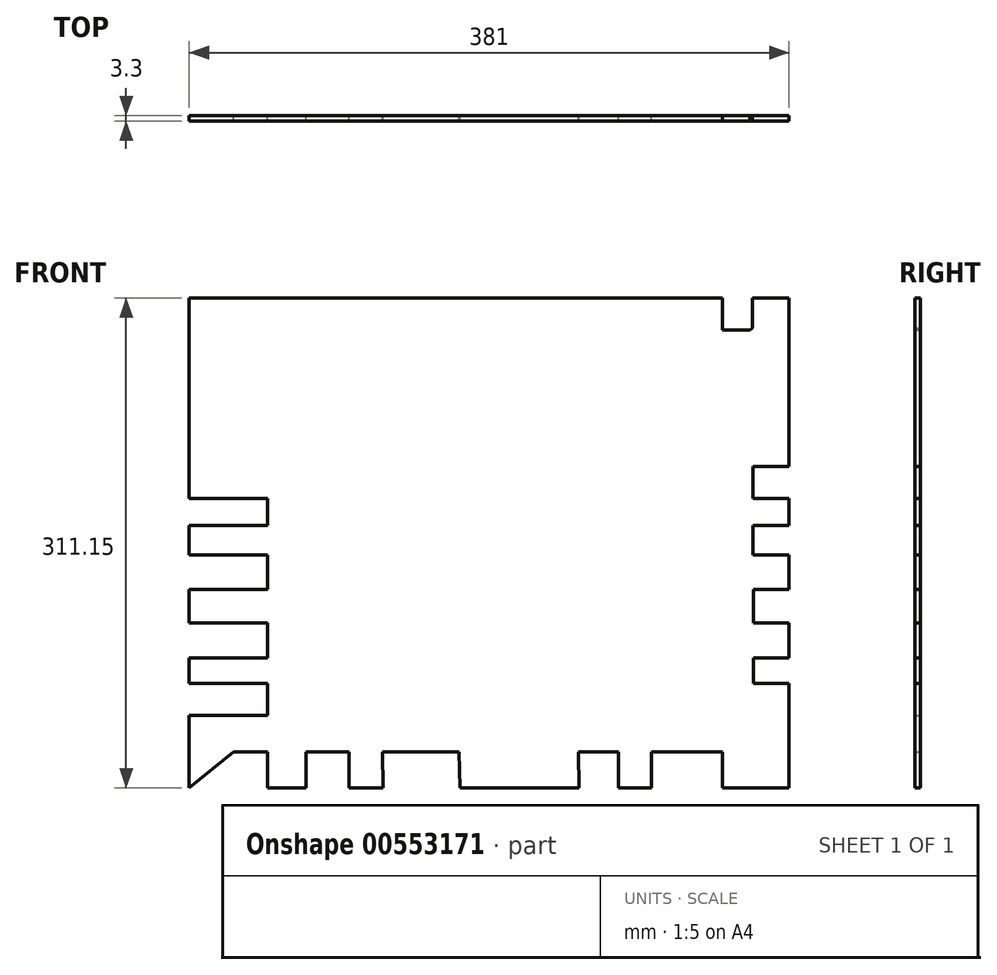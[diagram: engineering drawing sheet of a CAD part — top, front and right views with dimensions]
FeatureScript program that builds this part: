
annotation { "Feature Type Name" : "Feature", "Feature Type Description" : "" }
export const myFeature = defineFeature(function(context is Context, id is Id, definition is map)
    precondition{}
    {
        {
            var Q0;
            Q0=qCreatedBy(makeId("Front.planeOp"),FACE);
            var sketch = newSketch(context, id + "F0", { "sketchPlane" : qUnion([Q0])});
            skLineSegment(sketch, "E0.bottom", {"start": v(190.5, 155.58) * mm, "end": v(-190.5, 155.58) * mm});
            skLineSegment(sketch, "E0.top", {"start": v(190.5, -155.58) * mm, "end": v(-190.5, -155.58) * mm});
            skLineSegment(sketch, "E0.left", {"start": v(190.5, 155.58) * mm, "end": v(190.5, -155.58) * mm});
            skLineSegment(sketch, "E0.right", {"start": v(-190.5, 155.58) * mm, "end": v(-190.5, -155.58) * mm});
            skPoint(sketch, "E0.middle", {"position": v(0, 0) * mm});
            skLineSegment(sketch, "E1", {"start": v(-190.5, 155.58) * mm, "end": v(190.5, -155.57) * mm});
            skLineSegment(sketch, "E2", {"start": v(-190.5, -155.58) * mm, "end": v(190.5, 155.58) * mm});
            skLineSegment(sketch, "E3", {"start": v(-190.5, 135.33) * mm, "end": v(190.5, 135.33) * mm});
            skLineSegment(sketch, "E4", {"start": v(-190.5, 112.36) * mm, "end": v(190.5, 112.36) * mm});
            skLineSegment(sketch, "E5", {"start": v(-190.5, 91.1) * mm, "end": v(190.5, 91.1) * mm});
            skLineSegment(sketch, "E6", {"start": v(-190.5, 70.67) * mm, "end": v(190.5, 70.67) * mm});
            skLineSegment(sketch, "E7", {"start": v(-190.5, 48.55) * mm, "end": v(190.5, 48.55) * mm});
            skLineSegment(sketch, "E8", {"start": v(190.5, 48.55) * mm, "end": v(190.5, 28.13) * mm});
            skLineSegment(sketch, "E9", {"start": v(190.5, 28.13) * mm, "end": v(-190.5, 28.13) * mm});
            skLineSegment(sketch, "E10", {"start": v(-190.5, 28.13) * mm, "end": v(-190.5, 11.12) * mm});
            skLineSegment(sketch, "E11", {"start": v(-190.5, 11.12) * mm, "end": v(190.5, 11.12) * mm});
            skLineSegment(sketch, "E12", {"start": v(190.5, 11.12) * mm, "end": v(190.5, -7.6) * mm});
            skLineSegment(sketch, "E13", {"start": v(190.5, -7.6) * mm, "end": v(-190.5, -7.6) * mm});
            skLineSegment(sketch, "E14", {"start": v(-190.5, -7.6) * mm, "end": v(-190.5, -29.72) * mm});
            skLineSegment(sketch, "E15", {"start": v(-190.5, -29.72) * mm, "end": v(190.5, -29.72) * mm});
            skLineSegment(sketch, "E16", {"start": v(190.5, -29.72) * mm, "end": v(190.5, -50.99) * mm});
            skLineSegment(sketch, "E17", {"start": v(190.5, -50.99) * mm, "end": v(-190.5, -50.99) * mm});
            skLineSegment(sketch, "E18", {"start": v(-190.5, -50.99) * mm, "end": v(-190.5, -73.1) * mm});
            skLineSegment(sketch, "E19", {"start": v(-190.5, -73.1) * mm, "end": v(190.5, -73.1) * mm});
            skLineSegment(sketch, "E20", {"start": v(190.5, -73.1) * mm, "end": v(190.5, -89.27) * mm});
            skLineSegment(sketch, "E21", {"start": v(190.5, -89.27) * mm, "end": v(-190.5, -89.27) * mm});
            skLineSegment(sketch, "E22", {"start": v(-190.5, -89.27) * mm, "end": v(-190.5, -109.69) * mm});
            skLineSegment(sketch, "E23", {"start": v(-190.5, -109.69) * mm, "end": v(190.5, -109.69) * mm});
            skLineSegment(sketch, "E24", {"start": v(-190.5, -132.66) * mm, "end": v(190.5, -132.66) * mm});
            skLineSegment(sketch, "E25", {"start": v(96.32, 155.58) * mm, "end": v(50.38, 155.58) * mm});
            skLineSegment(sketch, "E26", {"start": v(9.5, 155.58) * mm, "end": v(-36.4, 155.58) * mm});
            skLineSegment(sketch, "E27", {"start": v(-81.1, 155.58) * mm, "end": v(-116.39, 155.58) * mm});
            skLineSegment(sketch, "E28", {"start": v(148.22, -155.58) * mm, "end": v(103.13, -155.58) * mm});
            skLineSegment(sketch, "E29", {"start": v(57.18, -155.58) * mm, "end": v(7.83, -155.58) * mm});
            skLineSegment(sketch, "E30", {"start": v(-35.56, -155.58) * mm, "end": v(-81.1, -155.58) * mm});
            skLineSegment(sketch, "E31", {"start": v(168.09, -155.58) * mm, "end": v(141.17, -155.58) * mm});
            skLineSegment(sketch, "E32", {"start": v(148.22, 155.58) * mm, "end": v(125.53, 155.58) * mm});
            skLineSegment(sketch, "E33", {"start": v(125.53, -155.58) * mm, "end": v(103.13, -155.58) * mm});
            skLineSegment(sketch, "E34", {"start": v(103.13, 155.58) * mm, "end": v(82.1, 155.58) * mm});
            skLineSegment(sketch, "E35", {"start": v(82.1, -155.58) * mm, "end": v(63.87, -155.58) * mm});
            skLineSegment(sketch, "E36", {"start": v(159.4, 155.58) * mm, "end": v(136.88, 155.58) * mm});
            skLineSegment(sketch, "E37", {"start": v(136.88, 155.58) * mm, "end": v(111.64, 155.58) * mm});
            skLineSegment(sketch, "E38", {"start": v(111.64, 155.58) * mm, "end": v(82.1, 155.58) * mm});
            skLineSegment(sketch, "E39", {"start": v(65.6, 155.58) * mm, "end": v(37.82, 155.58) * mm});
            skLineSegment(sketch, "E40", {"start": v(37.82, 155.58) * mm, "end": v(9.5, 155.58) * mm});
            skLineSegment(sketch, "E41", {"start": v(-13.45, 155.58) * mm, "end": v(-36.4, 155.58) * mm});
            skLineSegment(sketch, "E42", {"start": v(-63.8, 155.58) * mm, "end": v(-98.74, 155.58) * mm});
            skLineSegment(sketch, "E43", {"start": v(-98.74, 155.58) * mm, "end": v(-128.06, 155.58) * mm});
            skLineSegment(sketch, "E44", {"start": v(-128.06, 155.58) * mm, "end": v(-153.25, 155.58) * mm});
            skLineSegment(sketch, "E45", {"start": v(-153.25, 155.58) * mm, "end": v(-169.75, 155.58) * mm});
            skLineSegment(sketch, "E46", {"start": v(-169.75, 155.58) * mm, "end": v(159.4, 155.58) * mm});
            skLineSegment(sketch, "E47", {"start": v(167.22, 155.58) * mm, "end": v(168.09, -155.58) * mm});
            skLineSegment(sketch, "E48", {"start": v(148.22, 155.58) * mm, "end": v(148.22, -155.58) * mm});
            skLineSegment(sketch, "E49", {"start": v(125.53, 155.58) * mm, "end": v(125.53, -155.58) * mm});
            skLineSegment(sketch, "E50", {"start": v(103.13, 155.58) * mm, "end": v(103.13, -155.58) * mm});
            skLineSegment(sketch, "E51", {"start": v(82.1, 155.58) * mm, "end": v(82.1, -155.58) * mm});
            skLineSegment(sketch, "E52", {"start": v(50.38, 155.58) * mm, "end": v(57.18, -155.57) * mm});
            skLineSegment(sketch, "E53", {"start": v(23.66, 155.58) * mm, "end": v(32.5, -155.58) * mm});
            skLineSegment(sketch, "E54", {"start": v(0, 155.58) * mm, "end": v(7.83, -155.58) * mm});
            skLineSegment(sketch, "E55", {"start": v(-24.93, 155.58) * mm, "end": v(-18.64, -155.58) * mm});
            skLineSegment(sketch, "E56", {"start": v(-44.7, -155.58) * mm, "end": v(-67.27, -155.58) * mm});
            skLineSegment(sketch, "E57", {"start": v(-88.98, -155.58) * mm, "end": v(-108.96, -155.58) * mm});
            skLineSegment(sketch, "E58", {"start": v(-108.96, 155.58) * mm, "end": v(-128.06, 155.58) * mm});
            skLineSegment(sketch, "E59", {"start": v(-153.25, -155.58) * mm, "end": v(-174.1, -155.58) * mm});
            skLineSegment(sketch, "E60", {"start": v(-50.77, 155.58) * mm, "end": v(-44.7, -155.58) * mm});
            skLineSegment(sketch, "E61", {"start": v(-72.48, 155.58) * mm, "end": v(-67.27, -155.58) * mm});
            skLineSegment(sketch, "E62", {"start": v(-89.85, 155.58) * mm, "end": v(-88.98, -155.58) * mm});
            skLineSegment(sketch, "E63", {"start": v(-116.39, 155.58) * mm, "end": v(-116.39, -155.58) * mm});
            skLineSegment(sketch, "E64", {"start": v(-140.66, 155.58) * mm, "end": v(-140.66, -155.58) * mm});
            skSolve(sketch);
        }
        {
            var Q0;
            {var subQ0=sQuery(id+"F0.wireOp",EDGE,"E60");var subQ1=sQuery(id+"F0.wireOp",EDGE,"E13");var subQ2=makeQuery(id+"F0.imprint","INTERSECT",VERTEX,{"derivedFrom":[subQ1,subQ0]});Q0=makeQuery(id+"F0.imprint","IMPRINT",FACE,{"disambiguationData":[TD([[makeQuery(id+"F0.imprint","IMPRINT",EDGE,{"disambiguationData":[TD([[subQ2,-1.0]])],"derivedFrom":subQ1}),1.0]])]});}
            var Q1;
            {var subQ0=sQuery(id+"F0.wireOp",EDGE,"E4");var subQ1=sQuery(id+"F0.wireOp",EDGE,"E0.left");var subQ2=makeQuery(id+"F0.imprint","INTERSECT",VERTEX,{"derivedFrom":[subQ1,subQ0]});Q1=makeQuery(id+"F0.imprint","IMPRINT",FACE,{"disambiguationData":[TD([[makeQuery(id+"F0.imprint","IMPRINT",EDGE,{"disambiguationData":[TD([[subQ2,-1.0]])],"derivedFrom":subQ1}),-1.0]])]});}
            var Q2;
            {var subQ0=sQuery(id+"F0.wireOp",EDGE,"E54");var subQ1=sQuery(id+"F0.wireOp",EDGE,"E23");var subQ2=makeQuery(id+"F0.imprint","INTERSECT",VERTEX,{"derivedFrom":[subQ1,subQ0]});Q2=makeQuery(id+"F0.imprint","IMPRINT",FACE,{"disambiguationData":[TD([[makeQuery(id+"F0.imprint","IMPRINT",EDGE,{"disambiguationData":[TD([[subQ2,-1.0]])],"derivedFrom":subQ1}),-1.0]])]});}
            var Q3;
            {var subQ0=sQuery(id+"F0.wireOp",EDGE,"E52");var subQ1=sQuery(id+"F0.wireOp",EDGE,"E19");var subQ2=makeQuery(id+"F0.imprint","INTERSECT",VERTEX,{"derivedFrom":[subQ1,subQ0]});Q3=makeQuery(id+"F0.imprint","IMPRINT",FACE,{"disambiguationData":[TD([[makeQuery(id+"F0.imprint","IMPRINT",EDGE,{"disambiguationData":[TD([[subQ2,-1.0]])],"derivedFrom":subQ1}),-1.0]])]});}
            var Q4;
            {var subQ0=sQuery(id+"F0.wireOp",EDGE,"E60");var subQ1=sQuery(id+"F0.wireOp",EDGE,"E6");var subQ2=makeQuery(id+"F0.imprint","INTERSECT",VERTEX,{"derivedFrom":[subQ1,subQ0]});Q4=makeQuery(id+"F0.imprint","IMPRINT",FACE,{"disambiguationData":[TD([[makeQuery(id+"F0.imprint","IMPRINT",EDGE,{"disambiguationData":[TD([[subQ2,-1.0]])],"derivedFrom":subQ1}),-1.0]])]});}
            var Q5;
            {var subQ0=sQuery(id+"F0.wireOp",EDGE,"E48");var subQ1=sQuery(id+"F0.wireOp",EDGE,"E17");var subQ2=makeQuery(id+"F0.imprint","INTERSECT",VERTEX,{"derivedFrom":[subQ1,subQ0]});Q5=makeQuery(id+"F0.imprint","IMPRINT",FACE,{"disambiguationData":[TD([[makeQuery(id+"F0.imprint","IMPRINT",EDGE,{"disambiguationData":[TD([[subQ2,-1.0]])],"derivedFrom":subQ1}),1.0]])]});}
            var Q6;
            {var subQ0=sQuery(id+"F0.wireOp",EDGE,"E53");var subQ1=sQuery(id+"F0.wireOp",EDGE,"E4");var subQ2=makeQuery(id+"F0.imprint","INTERSECT",VERTEX,{"derivedFrom":[subQ1,subQ0]});Q6=makeQuery(id+"F0.imprint","IMPRINT",FACE,{"disambiguationData":[TD([[makeQuery(id+"F0.imprint","IMPRINT",EDGE,{"disambiguationData":[TD([[subQ2,-1.0]])],"derivedFrom":subQ1}),-1.0]])]});}
            var Q7;
            {var subQ0=sQuery(id+"F0.wireOp",EDGE,"E6");var subQ1=sQuery(id+"F0.wireOp",EDGE,"E2");var subQ2=makeQuery(id+"F0.imprint","INTERSECT",VERTEX,{"derivedFrom":[subQ1,subQ0]});Q7=makeQuery(id+"F0.imprint","IMPRINT",FACE,{"disambiguationData":[TD([[makeQuery(id+"F0.imprint","IMPRINT",EDGE,{"disambiguationData":[TD([[subQ2,-1.0]])],"derivedFrom":subQ1}),-1.0]])]});}
            var Q8;
            {var subQ0=sQuery(id+"F0.wireOp",EDGE,"E53");var subQ1=sQuery(id+"F0.wireOp",EDGE,"E11");var subQ2=makeQuery(id+"F0.imprint","INTERSECT",VERTEX,{"derivedFrom":[subQ1,subQ0]});Q8=makeQuery(id+"F0.imprint","IMPRINT",FACE,{"disambiguationData":[TD([[makeQuery(id+"F0.imprint","IMPRINT",EDGE,{"disambiguationData":[TD([[subQ2,-1.0]])],"derivedFrom":subQ1}),-1.0]])]});}
            var Q9;
            {var subQ0=sQuery(id+"F0.wireOp",EDGE,"E54");var subQ1=sQuery(id+"F0.wireOp",EDGE,"E19");var subQ2=makeQuery(id+"F0.imprint","INTERSECT",VERTEX,{"derivedFrom":[subQ1,subQ0]});Q9=makeQuery(id+"F0.imprint","IMPRINT",FACE,{"disambiguationData":[TD([[makeQuery(id+"F0.imprint","IMPRINT",EDGE,{"disambiguationData":[TD([[subQ2,-1.0]])],"derivedFrom":subQ1}),-1.0]])]});}
            var Q10;
            {var subQ0=sQuery(id+"F0.wireOp",EDGE,"E15");var subQ1=sQuery(id+"F0.wireOp",EDGE,"E2");var subQ2=makeQuery(id+"F0.imprint","INTERSECT",VERTEX,{"derivedFrom":[subQ1,subQ0]});Q10=makeQuery(id+"F0.imprint","IMPRINT",FACE,{"disambiguationData":[TD([[makeQuery(id+"F0.imprint","IMPRINT",EDGE,{"disambiguationData":[TD([[subQ2,-1.0]])],"derivedFrom":subQ1}),-1.0]])]});}
            var Q11;
            {var subQ0=sQuery(id+"F0.wireOp",EDGE,"E52");var subQ1=sQuery(id+"F0.wireOp",EDGE,"E3");var subQ2=makeQuery(id+"F0.imprint","INTERSECT",VERTEX,{"derivedFrom":[subQ1,subQ0]});Q11=makeQuery(id+"F0.imprint","IMPRINT",FACE,{"disambiguationData":[TD([[makeQuery(id+"F0.imprint","IMPRINT",EDGE,{"disambiguationData":[TD([[subQ2,-1.0]])],"derivedFrom":subQ1}),1.0]])]});}
            var Q12;
            {var subQ0=sQuery(id+"F0.wireOp",EDGE,"E53");var subQ1=sQuery(id+"F0.wireOp",EDGE,"E19");var subQ2=makeQuery(id+"F0.imprint","INTERSECT",VERTEX,{"derivedFrom":[subQ1,subQ0]});Q12=makeQuery(id+"F0.imprint","IMPRINT",FACE,{"disambiguationData":[TD([[makeQuery(id+"F0.imprint","IMPRINT",EDGE,{"disambiguationData":[TD([[subQ2,-1.0]])],"derivedFrom":subQ1}),-1.0]])]});}
            var Q13;
            {var subQ0=sQuery(id+"F0.wireOp",EDGE,"E5");var subQ1=sQuery(id+"F0.wireOp",EDGE,"E1");var subQ2=makeQuery(id+"F0.imprint","INTERSECT",VERTEX,{"derivedFrom":[subQ1,subQ0]});Q13=makeQuery(id+"F0.imprint","IMPRINT",FACE,{"disambiguationData":[TD([[makeQuery(id+"F0.imprint","IMPRINT",EDGE,{"disambiguationData":[TD([[subQ2,-1.0]])],"derivedFrom":subQ1}),1.0]])]});}
            var Q14;
            {var subQ0=sQuery(id+"F0.wireOp",EDGE,"E47");var subQ1=sQuery(id+"F0.wireOp",EDGE,"E21");var subQ2=makeQuery(id+"F0.imprint","INTERSECT",VERTEX,{"derivedFrom":[subQ1,subQ0]});Q14=makeQuery(id+"F0.imprint","IMPRINT",FACE,{"disambiguationData":[TD([[makeQuery(id+"F0.imprint","IMPRINT",EDGE,{"disambiguationData":[TD([[subQ2,-1.0]])],"derivedFrom":subQ1}),1.0]])]});}
            var Q15;
            {var subQ0=sQuery(id+"F0.wireOp",EDGE,"E50");var subQ1=sQuery(id+"F0.wireOp",EDGE,"E7");var subQ2=makeQuery(id+"F0.imprint","INTERSECT",VERTEX,{"derivedFrom":[subQ1,subQ0]});Q15=makeQuery(id+"F0.imprint","IMPRINT",FACE,{"disambiguationData":[TD([[makeQuery(id+"F0.imprint","IMPRINT",EDGE,{"disambiguationData":[TD([[subQ2,-1.0]])],"derivedFrom":subQ1}),-1.0]])]});}
            var Q16;
            {var subQ1=sQuery(id+"F0.wireOp",EDGE,"E2");var subQ7=sQuery(id+"F0.wireOp",EDGE,"E6");var subQ8=makeQuery(id+"F0.imprint","INTERSECT",VERTEX,{"derivedFrom":[subQ1,subQ7]});Q16=makeQuery(id+"F0.imprint","IMPRINT",FACE,{"disambiguationData":[TD([[makeQuery(id+"F0.imprint","IMPRINT",EDGE,{"disambiguationData":[TD([[subQ8,-1.0]])],"derivedFrom":subQ1}),1.0]])]});}
            var Q17;
            {var subQ5=sQuery(id+"F0.wireOp",EDGE,"E46");var subQ6=sQuery(id+"F0.wireOp",EDGE,"E0.bottom");var subQ7=makeQuery(id+"F0.imprint","INTERSECT",VERTEX,{"disambiguationData":[OD(1.0)],"derivedFrom":[subQ6,subQ5]});Q17=makeQuery(id+"F0.imprint","IMPRINT",FACE,{"disambiguationData":[TD([[makeQuery(id+"F0.imprint","IMPRINT",EDGE,{"disambiguationData":[TD([[subQ7,1.0]])],"derivedFrom":subQ6}),1.0]])]});}
            var Q18;
            {var subQ0=sQuery(id+"F0.wireOp",EDGE,"E11");var subQ5=sQuery(id+"F0.wireOp",EDGE,"E64");var subQ6=makeQuery(id+"F0.imprint","INTERSECT",VERTEX,{"derivedFrom":[subQ0,subQ5]});Q18=makeQuery(id+"F0.imprint","IMPRINT",FACE,{"disambiguationData":[TD([[makeQuery(id+"F0.imprint","IMPRINT",EDGE,{"disambiguationData":[TD([[subQ6,-1.0]])],"derivedFrom":subQ5}),-1.0]])]});}
            var Q19;
            {var subQ0=sQuery(id+"F0.wireOp",EDGE,"E51");var subQ1=sQuery(id+"F0.wireOp",EDGE,"E3");var subQ2=makeQuery(id+"F0.imprint","INTERSECT",VERTEX,{"derivedFrom":[subQ1,subQ0]});Q19=makeQuery(id+"F0.imprint","IMPRINT",FACE,{"disambiguationData":[TD([[makeQuery(id+"F0.imprint","IMPRINT",EDGE,{"disambiguationData":[TD([[subQ2,-1.0]])],"derivedFrom":subQ1}),1.0]])]});}
            var Q20;
            {var subQ5=sQuery(id+"F0.wireOp",EDGE,"E1");var subQ7=sQuery(id+"F0.wireOp",EDGE,"E63");var subQ9=makeQuery(id+"F0.imprint","INTERSECT",VERTEX,{"derivedFrom":[subQ5,subQ7]});Q20=makeQuery(id+"F0.imprint","IMPRINT",FACE,{"disambiguationData":[TD([[makeQuery(id+"F0.imprint","IMPRINT",EDGE,{"disambiguationData":[TD([[subQ9,-1.0]])],"derivedFrom":subQ5}),1.0]])]});}
            var Q21;
            {var subQ0=sQuery(id+"F0.wireOp",EDGE,"E48");var subQ1=sQuery(id+"F0.wireOp",EDGE,"E7");var subQ2=makeQuery(id+"F0.imprint","INTERSECT",VERTEX,{"derivedFrom":[subQ1,subQ0]});Q21=makeQuery(id+"F0.imprint","IMPRINT",FACE,{"disambiguationData":[TD([[makeQuery(id+"F0.imprint","IMPRINT",EDGE,{"disambiguationData":[TD([[subQ2,-1.0]])],"derivedFrom":subQ1}),-1.0]])]});}
            var Q22;
            {var subQ0=sQuery(id+"F0.wireOp",EDGE,"E12");Q22=makeQuery(id+"F0.imprint","IMPRINT",FACE,{"disambiguationData":[TD([[makeQuery(id+"F0.imprint","IMPRINT",EDGE,{"derivedFrom":subQ0}),-1.0]])]});}
            var Q23;
            {var subQ0=sQuery(id+"F0.wireOp",EDGE,"E24");var subQ3=sQuery(id+"F0.wireOp",EDGE,"E2");var subQ4=makeQuery(id+"F0.imprint","INTERSECT",VERTEX,{"derivedFrom":[subQ3,subQ0]});Q23=makeQuery(id+"F0.imprint","IMPRINT",FACE,{"disambiguationData":[TD([[makeQuery(id+"F0.imprint","IMPRINT",EDGE,{"disambiguationData":[TD([[subQ4,-1.0]])],"derivedFrom":subQ3}),1.0]])]});}
            var Q24;
            {var subQ0=sQuery(id+"F0.wireOp",EDGE,"E52");var subQ1=sQuery(id+"F0.wireOp",EDGE,"E11");var subQ2=makeQuery(id+"F0.imprint","INTERSECT",VERTEX,{"derivedFrom":[subQ1,subQ0]});Q24=makeQuery(id+"F0.imprint","IMPRINT",FACE,{"disambiguationData":[TD([[makeQuery(id+"F0.imprint","IMPRINT",EDGE,{"disambiguationData":[TD([[subQ2,-1.0]])],"derivedFrom":subQ1}),-1.0]])]});}
            var Q25;
            {var subQ3=sQuery(id+"F0.wireOp",EDGE,"E24");var subQ7=sQuery(id+"F0.wireOp",EDGE,"E62");var subQ8=makeQuery(id+"F0.imprint","INTERSECT",VERTEX,{"derivedFrom":[subQ3,subQ7]});Q25=makeQuery(id+"F0.imprint","IMPRINT",FACE,{"disambiguationData":[TD([[makeQuery(id+"F0.imprint","IMPRINT",EDGE,{"disambiguationData":[TD([[subQ8,-1.0]])],"derivedFrom":subQ3}),-1.0]])]});}
            var Q26;
            {var subQ1=sQuery(id+"F0.wireOp",EDGE,"E1");var subQ7=sQuery(id+"F0.wireOp",EDGE,"E19");var subQ8=makeQuery(id+"F0.imprint","INTERSECT",VERTEX,{"derivedFrom":[subQ1,subQ7]});Q26=makeQuery(id+"F0.imprint","IMPRINT",FACE,{"disambiguationData":[TD([[makeQuery(id+"F0.imprint","IMPRINT",EDGE,{"disambiguationData":[TD([[subQ8,-1.0]])],"derivedFrom":subQ1}),-1.0]])]});}
            var Q27;
            {var subQ0=sQuery(id+"F0.wireOp",EDGE,"E61");var subQ1=sQuery(id+"F0.wireOp",EDGE,"E21");var subQ2=makeQuery(id+"F0.imprint","INTERSECT",VERTEX,{"derivedFrom":[subQ1,subQ0]});Q27=makeQuery(id+"F0.imprint","IMPRINT",FACE,{"disambiguationData":[TD([[makeQuery(id+"F0.imprint","IMPRINT",EDGE,{"disambiguationData":[TD([[subQ2,-1.0]])],"derivedFrom":subQ1}),1.0]])]});}
            var Q28;
            {var subQ0=sQuery(id+"F0.wireOp",EDGE,"E24");var subQ1=sQuery(id+"F0.wireOp",EDGE,"E2");var subQ2=makeQuery(id+"F0.imprint","INTERSECT",VERTEX,{"derivedFrom":[subQ1,subQ0]});Q28=makeQuery(id+"F0.imprint","IMPRINT",FACE,{"disambiguationData":[TD([[makeQuery(id+"F0.imprint","IMPRINT",EDGE,{"disambiguationData":[TD([[subQ2,-1.0]])],"derivedFrom":subQ1}),-1.0]])]});}
            var Q29;
            {var subQ0=sQuery(id+"F0.wireOp",EDGE,"E23");var subQ1=sQuery(id+"F0.wireOp",EDGE,"E0.left");var subQ2=makeQuery(id+"F0.imprint","INTERSECT",VERTEX,{"derivedFrom":[subQ1,subQ0]});Q29=makeQuery(id+"F0.imprint","IMPRINT",FACE,{"disambiguationData":[TD([[makeQuery(id+"F0.imprint","IMPRINT",EDGE,{"disambiguationData":[TD([[subQ2,-1.0]])],"derivedFrom":subQ1}),-1.0]])]});}
            var Q30;
            {var subQ0=sQuery(id+"F0.wireOp",EDGE,"E60");var subQ1=sQuery(id+"F0.wireOp",EDGE,"E5");var subQ2=makeQuery(id+"F0.imprint","INTERSECT",VERTEX,{"derivedFrom":[subQ1,subQ0]});Q30=makeQuery(id+"F0.imprint","IMPRINT",FACE,{"disambiguationData":[TD([[makeQuery(id+"F0.imprint","IMPRINT",EDGE,{"disambiguationData":[TD([[subQ2,-1.0]])],"derivedFrom":subQ1}),-1.0]])]});}
            var Q31;
            {var subQ0=sQuery(id+"F0.wireOp",EDGE,"E62");var subQ1=sQuery(id+"F0.wireOp",EDGE,"E3");var subQ2=makeQuery(id+"F0.imprint","INTERSECT",VERTEX,{"derivedFrom":[subQ1,subQ0]});Q31=makeQuery(id+"F0.imprint","IMPRINT",FACE,{"disambiguationData":[TD([[makeQuery(id+"F0.imprint","IMPRINT",EDGE,{"disambiguationData":[TD([[subQ2,-1.0]])],"derivedFrom":subQ1}),1.0]])]});}
            var Q32;
            {var subQ0=sQuery(id+"F0.wireOp",EDGE,"E4");var subQ1=sQuery(id+"F0.wireOp",EDGE,"E1");var subQ2=makeQuery(id+"F0.imprint","INTERSECT",VERTEX,{"derivedFrom":[subQ1,subQ0]});Q32=makeQuery(id+"F0.imprint","IMPRINT",FACE,{"disambiguationData":[TD([[makeQuery(id+"F0.imprint","IMPRINT",EDGE,{"disambiguationData":[TD([[subQ2,-1.0]])],"derivedFrom":subQ1}),1.0]])]});}
            var Q33;
            {var subQ0=sQuery(id+"F0.wireOp",EDGE,"E53");var subQ1=sQuery(id+"F0.wireOp",EDGE,"E23");var subQ2=makeQuery(id+"F0.imprint","INTERSECT",VERTEX,{"derivedFrom":[subQ1,subQ0]});Q33=makeQuery(id+"F0.imprint","IMPRINT",FACE,{"disambiguationData":[TD([[makeQuery(id+"F0.imprint","IMPRINT",EDGE,{"disambiguationData":[TD([[subQ2,-1.0]])],"derivedFrom":subQ1}),-1.0]])]});}
            var Q34;
            {var subQ0=sQuery(id+"F0.wireOp",EDGE,"E50");var subQ1=sQuery(id+"F0.wireOp",EDGE,"E21");var subQ2=makeQuery(id+"F0.imprint","INTERSECT",VERTEX,{"derivedFrom":[subQ1,subQ0]});Q34=makeQuery(id+"F0.imprint","IMPRINT",FACE,{"disambiguationData":[TD([[makeQuery(id+"F0.imprint","IMPRINT",EDGE,{"disambiguationData":[TD([[subQ2,-1.0]])],"derivedFrom":subQ1}),1.0]])]});}
            var Q35;
            {var subQ0=sQuery(id+"F0.wireOp",EDGE,"E60");var subQ1=sQuery(id+"F0.wireOp",EDGE,"E21");var subQ2=makeQuery(id+"F0.imprint","INTERSECT",VERTEX,{"derivedFrom":[subQ1,subQ0]});Q35=makeQuery(id+"F0.imprint","IMPRINT",FACE,{"disambiguationData":[TD([[makeQuery(id+"F0.imprint","IMPRINT",EDGE,{"disambiguationData":[TD([[subQ2,-1.0]])],"derivedFrom":subQ1}),1.0]])]});}
            var Q36;
            {var subQ0=sQuery(id+"F0.wireOp",EDGE,"E51");var subQ1=sQuery(id+"F0.wireOp",EDGE,"E11");var subQ2=makeQuery(id+"F0.imprint","INTERSECT",VERTEX,{"derivedFrom":[subQ1,subQ0]});Q36=makeQuery(id+"F0.imprint","IMPRINT",FACE,{"disambiguationData":[TD([[makeQuery(id+"F0.imprint","IMPRINT",EDGE,{"disambiguationData":[TD([[subQ2,-1.0]])],"derivedFrom":subQ1}),-1.0]])]});}
            var Q37;
            {var subQ5=sQuery(id+"F0.wireOp",EDGE,"E50");var subQ6=sQuery(id+"F0.wireOp",EDGE,"E1");var subQ7=makeQuery(id+"F0.imprint","INTERSECT",VERTEX,{"derivedFrom":[subQ6,subQ5]});Q37=makeQuery(id+"F0.imprint","IMPRINT",FACE,{"disambiguationData":[TD([[makeQuery(id+"F0.imprint","IMPRINT",EDGE,{"disambiguationData":[TD([[subQ7,-1.0]])],"derivedFrom":subQ6}),1.0]])]});}
            var Q38;
            {var subQ0=sQuery(id+"F0.wireOp",EDGE,"E54");var subQ1=sQuery(id+"F0.wireOp",EDGE,"E6");var subQ2=makeQuery(id+"F0.imprint","INTERSECT",VERTEX,{"derivedFrom":[subQ1,subQ0]});Q38=makeQuery(id+"F0.imprint","IMPRINT",FACE,{"disambiguationData":[TD([[makeQuery(id+"F0.imprint","IMPRINT",EDGE,{"disambiguationData":[TD([[subQ2,-1.0]])],"derivedFrom":subQ1}),-1.0]])]});}
            var Q39;
            {var subQ1=sQuery(id+"F0.wireOp",EDGE,"E1");var subQ7=sQuery(id+"F0.wireOp",EDGE,"E53");var subQ9=makeQuery(id+"F0.imprint","INTERSECT",VERTEX,{"derivedFrom":[subQ1,subQ7]});Q39=makeQuery(id+"F0.imprint","IMPRINT",FACE,{"disambiguationData":[TD([[makeQuery(id+"F0.imprint","IMPRINT",EDGE,{"disambiguationData":[TD([[subQ9,-1.0]])],"derivedFrom":subQ1}),1.0]])]});}
            var Q40;
            {var subQ0=sQuery(id+"F0.wireOp",EDGE,"E62");var subQ1=sQuery(id+"F0.wireOp",EDGE,"E13");var subQ2=makeQuery(id+"F0.imprint","INTERSECT",VERTEX,{"derivedFrom":[subQ1,subQ0]});Q40=makeQuery(id+"F0.imprint","IMPRINT",FACE,{"disambiguationData":[TD([[makeQuery(id+"F0.imprint","IMPRINT",EDGE,{"disambiguationData":[TD([[subQ2,-1.0]])],"derivedFrom":subQ1}),1.0]])]});}
            var Q41;
            {var subQ3=sQuery(id+"F0.wireOp",EDGE,"E3");var subQ7=sQuery(id+"F0.wireOp",EDGE,"E63");var subQ9=makeQuery(id+"F0.imprint","INTERSECT",VERTEX,{"derivedFrom":[subQ3,subQ7]});Q41=makeQuery(id+"F0.imprint","IMPRINT",FACE,{"disambiguationData":[TD([[makeQuery(id+"F0.imprint","IMPRINT",EDGE,{"disambiguationData":[TD([[subQ9,-1.0]])],"derivedFrom":subQ3}),1.0]])]});}
            var Q42;
            {var subQ0=sQuery(id+"F0.wireOp",EDGE,"E48");var subQ1=sQuery(id+"F0.wireOp",EDGE,"E9");var subQ2=makeQuery(id+"F0.imprint","INTERSECT",VERTEX,{"derivedFrom":[subQ1,subQ0]});Q42=makeQuery(id+"F0.imprint","IMPRINT",FACE,{"disambiguationData":[TD([[makeQuery(id+"F0.imprint","IMPRINT",EDGE,{"disambiguationData":[TD([[subQ2,-1.0]])],"derivedFrom":subQ1}),1.0]])]});}
            var Q43;
            {var subQ0=sQuery(id+"F0.wireOp",EDGE,"E49");var subQ1=sQuery(id+"F0.wireOp",EDGE,"E3");var subQ2=makeQuery(id+"F0.imprint","INTERSECT",VERTEX,{"derivedFrom":[subQ1,subQ0]});Q43=makeQuery(id+"F0.imprint","IMPRINT",FACE,{"disambiguationData":[TD([[makeQuery(id+"F0.imprint","IMPRINT",EDGE,{"disambiguationData":[TD([[subQ2,-1.0]])],"derivedFrom":subQ1}),1.0]])]});}
            var Q44;
            {var subQ0=sQuery(id+"F0.wireOp",EDGE,"E61");var subQ1=sQuery(id+"F0.wireOp",EDGE,"E5");var subQ2=makeQuery(id+"F0.imprint","INTERSECT",VERTEX,{"derivedFrom":[subQ1,subQ0]});Q44=makeQuery(id+"F0.imprint","IMPRINT",FACE,{"disambiguationData":[TD([[makeQuery(id+"F0.imprint","IMPRINT",EDGE,{"disambiguationData":[TD([[subQ2,-1.0]])],"derivedFrom":subQ1}),-1.0]])]});}
            var Q45;
            {var subQ0=sQuery(id+"F0.wireOp",EDGE,"E49");var subQ1=sQuery(id+"F0.wireOp",EDGE,"E15");var subQ2=makeQuery(id+"F0.imprint","INTERSECT",VERTEX,{"derivedFrom":[subQ1,subQ0]});Q45=makeQuery(id+"F0.imprint","IMPRINT",FACE,{"disambiguationData":[TD([[makeQuery(id+"F0.imprint","IMPRINT",EDGE,{"disambiguationData":[TD([[subQ2,-1.0]])],"derivedFrom":subQ1}),-1.0]])]});}
            var Q46;
            {var subQ0=sQuery(id+"F0.wireOp",EDGE,"E61");var subQ1=sQuery(id+"F0.wireOp",EDGE,"E3");var subQ2=makeQuery(id+"F0.imprint","INTERSECT",VERTEX,{"derivedFrom":[subQ1,subQ0]});Q46=makeQuery(id+"F0.imprint","IMPRINT",FACE,{"disambiguationData":[TD([[makeQuery(id+"F0.imprint","IMPRINT",EDGE,{"disambiguationData":[TD([[subQ2,-1.0]])],"derivedFrom":subQ1}),-1.0]])]});}
            var Q47;
            {var subQ0=sQuery(id+"F0.wireOp",EDGE,"E60");var subQ1=sQuery(id+"F0.wireOp",EDGE,"E9");var subQ2=makeQuery(id+"F0.imprint","INTERSECT",VERTEX,{"derivedFrom":[subQ1,subQ0]});Q47=makeQuery(id+"F0.imprint","IMPRINT",FACE,{"disambiguationData":[TD([[makeQuery(id+"F0.imprint","IMPRINT",EDGE,{"disambiguationData":[TD([[subQ2,-1.0]])],"derivedFrom":subQ1}),1.0]])]});}
            var Q48;
            {var subQ1=sQuery(id+"F0.wireOp",EDGE,"E2");var subQ7=sQuery(id+"F0.wireOp",EDGE,"E23");var subQ8=makeQuery(id+"F0.imprint","INTERSECT",VERTEX,{"derivedFrom":[subQ1,subQ7]});Q48=makeQuery(id+"F0.imprint","IMPRINT",FACE,{"disambiguationData":[TD([[makeQuery(id+"F0.imprint","IMPRINT",EDGE,{"disambiguationData":[TD([[subQ8,-1.0]])],"derivedFrom":subQ1}),1.0]])]});}
            var Q49;
            {var subQ0=sQuery(id+"F0.wireOp",EDGE,"E51");var subQ1=sQuery(id+"F0.wireOp",EDGE,"E13");var subQ2=makeQuery(id+"F0.imprint","INTERSECT",VERTEX,{"derivedFrom":[subQ1,subQ0]});Q49=makeQuery(id+"F0.imprint","IMPRINT",FACE,{"disambiguationData":[TD([[makeQuery(id+"F0.imprint","IMPRINT",EDGE,{"disambiguationData":[TD([[subQ2,-1.0]])],"derivedFrom":subQ1}),1.0]])]});}
            var Q50;
            {var subQ0=sQuery(id+"F0.wireOp",EDGE,"E17");var subQ1=sQuery(id+"F0.wireOp",EDGE,"E2");var subQ2=makeQuery(id+"F0.imprint","INTERSECT",VERTEX,{"derivedFrom":[subQ1,subQ0]});Q50=makeQuery(id+"F0.imprint","IMPRINT",FACE,{"disambiguationData":[TD([[makeQuery(id+"F0.imprint","IMPRINT",EDGE,{"disambiguationData":[TD([[subQ2,-1.0]])],"derivedFrom":subQ1}),-1.0]])]});}
            var Q51;
            {var subQ0=sQuery(id+"F0.wireOp",EDGE,"E47");var subQ1=sQuery(id+"F0.wireOp",EDGE,"E13");var subQ2=makeQuery(id+"F0.imprint","INTERSECT",VERTEX,{"derivedFrom":[subQ1,subQ0]});Q51=makeQuery(id+"F0.imprint","IMPRINT",FACE,{"disambiguationData":[TD([[makeQuery(id+"F0.imprint","IMPRINT",EDGE,{"disambiguationData":[TD([[subQ2,-1.0]])],"derivedFrom":subQ1}),1.0]])]});}
            var Q52;
            {var subQ0=sQuery(id+"F0.wireOp",EDGE,"E18");Q52=makeQuery(id+"F0.imprint","IMPRINT",FACE,{"disambiguationData":[TD([[makeQuery(id+"F0.imprint","IMPRINT",EDGE,{"derivedFrom":subQ0}),1.0]])]});}
            var Q53;
            {var subQ5=sQuery(id+"F0.wireOp",EDGE,"E2");var subQ7=sQuery(id+"F0.wireOp",EDGE,"E48");var subQ9=makeQuery(id+"F0.imprint","INTERSECT",VERTEX,{"derivedFrom":[subQ5,subQ7]});Q53=makeQuery(id+"F0.imprint","IMPRINT",FACE,{"disambiguationData":[TD([[makeQuery(id+"F0.imprint","IMPRINT",EDGE,{"disambiguationData":[TD([[subQ9,-1.0]])],"derivedFrom":subQ5}),-1.0]])]});}
            var Q54;
            {var subQ3=sQuery(id+"F0.wireOp",EDGE,"E51");var subQ5=sQuery(id+"F0.wireOp",EDGE,"E24");var subQ6=makeQuery(id+"F0.imprint","INTERSECT",VERTEX,{"derivedFrom":[subQ5,subQ3]});Q54=makeQuery(id+"F0.imprint","IMPRINT",FACE,{"disambiguationData":[TD([[makeQuery(id+"F0.imprint","IMPRINT",EDGE,{"disambiguationData":[TD([[subQ6,-1.0]])],"derivedFrom":subQ5}),-1.0]])]});}
            var Q55;
            {var subQ0=sQuery(id+"F0.wireOp",EDGE,"E62");var subQ1=sQuery(id+"F0.wireOp",EDGE,"E7");var subQ2=makeQuery(id+"F0.imprint","INTERSECT",VERTEX,{"derivedFrom":[subQ1,subQ0]});Q55=makeQuery(id+"F0.imprint","IMPRINT",FACE,{"disambiguationData":[TD([[makeQuery(id+"F0.imprint","IMPRINT",EDGE,{"disambiguationData":[TD([[subQ2,-1.0]])],"derivedFrom":subQ1}),-1.0]])]});}
            var Q56;
            {var subQ5=sQuery(id+"F0.wireOp",EDGE,"E33");Q56=makeQuery(id+"F0.imprint","IMPRINT",FACE,{"disambiguationData":[TD([[makeQuery(id+"F0.imprint","IMPRINT",EDGE,{"derivedFrom":subQ5}),-1.0]])]});}
            var Q57;
            {var subQ0=sQuery(id+"F0.wireOp",EDGE,"E64");var subQ1=sQuery(id+"F0.wireOp",EDGE,"E6");var subQ2=makeQuery(id+"F0.imprint","INTERSECT",VERTEX,{"derivedFrom":[subQ1,subQ0]});Q57=makeQuery(id+"F0.imprint","IMPRINT",FACE,{"disambiguationData":[TD([[makeQuery(id+"F0.imprint","IMPRINT",EDGE,{"disambiguationData":[TD([[subQ2,-1.0]])],"derivedFrom":subQ1}),-1.0]])]});}
            var Q58;
            {var subQ0=sQuery(id+"F0.wireOp",EDGE,"E8");Q58=makeQuery(id+"F0.imprint","IMPRINT",FACE,{"disambiguationData":[TD([[makeQuery(id+"F0.imprint","IMPRINT",EDGE,{"derivedFrom":subQ0}),-1.0]])]});}
            var Q59;
            {var subQ0=sQuery(id+"F0.wireOp",EDGE,"E55");var subQ1=sQuery(id+"F0.wireOp",EDGE,"E4");var subQ2=makeQuery(id+"F0.imprint","INTERSECT",VERTEX,{"derivedFrom":[subQ1,subQ0]});Q59=makeQuery(id+"F0.imprint","IMPRINT",FACE,{"disambiguationData":[TD([[makeQuery(id+"F0.imprint","IMPRINT",EDGE,{"disambiguationData":[TD([[subQ2,-1.0]])],"derivedFrom":subQ1}),-1.0]])]});}
            var Q60;
            {var subQ0=sQuery(id+"F0.wireOp",EDGE,"E54");var subQ1=sQuery(id+"F0.wireOp",EDGE,"E5");var subQ2=makeQuery(id+"F0.imprint","INTERSECT",VERTEX,{"derivedFrom":[subQ1,subQ0]});Q60=makeQuery(id+"F0.imprint","IMPRINT",FACE,{"disambiguationData":[TD([[makeQuery(id+"F0.imprint","IMPRINT",EDGE,{"disambiguationData":[TD([[subQ2,-1.0]])],"derivedFrom":subQ1}),-1.0]])]});}
            var Q61;
            {var subQ5=sQuery(id+"F0.wireOp",EDGE,"E1");var subQ7=sQuery(id+"F0.wireOp",EDGE,"E64");var subQ8=makeQuery(id+"F0.imprint","INTERSECT",VERTEX,{"derivedFrom":[subQ5,subQ7]});Q61=makeQuery(id+"F0.imprint","IMPRINT",FACE,{"disambiguationData":[TD([[makeQuery(id+"F0.imprint","IMPRINT",EDGE,{"disambiguationData":[TD([[subQ8,-1.0]])],"derivedFrom":subQ5}),1.0]])]});}
            var Q62;
            {var subQ0=sQuery(id+"F0.wireOp",EDGE,"E52");var subQ1=sQuery(id+"F0.wireOp",EDGE,"E17");var subQ2=makeQuery(id+"F0.imprint","INTERSECT",VERTEX,{"derivedFrom":[subQ1,subQ0]});Q62=makeQuery(id+"F0.imprint","IMPRINT",FACE,{"disambiguationData":[TD([[makeQuery(id+"F0.imprint","IMPRINT",EDGE,{"disambiguationData":[TD([[subQ2,-1.0]])],"derivedFrom":subQ1}),1.0]])]});}
            var Q63;
            {var subQ0=sQuery(id+"F0.wireOp",EDGE,"E48");var subQ1=sQuery(id+"F0.wireOp",EDGE,"E6");var subQ2=makeQuery(id+"F0.imprint","INTERSECT",VERTEX,{"derivedFrom":[subQ1,subQ0]});Q63=makeQuery(id+"F0.imprint","IMPRINT",FACE,{"disambiguationData":[TD([[makeQuery(id+"F0.imprint","IMPRINT",EDGE,{"disambiguationData":[TD([[subQ2,-1.0]])],"derivedFrom":subQ1}),-1.0]])]});}
            var Q64;
            {var subQ0=sQuery(id+"F0.wireOp",EDGE,"E53");var subQ1=sQuery(id+"F0.wireOp",EDGE,"E6");var subQ2=makeQuery(id+"F0.imprint","INTERSECT",VERTEX,{"derivedFrom":[subQ1,subQ0]});Q64=makeQuery(id+"F0.imprint","IMPRINT",FACE,{"disambiguationData":[TD([[makeQuery(id+"F0.imprint","IMPRINT",EDGE,{"disambiguationData":[TD([[subQ2,-1.0]])],"derivedFrom":subQ1}),-1.0]])]});}
            var Q65;
            {var subQ0=sQuery(id+"F0.wireOp",EDGE,"E48");var subQ1=sQuery(id+"F0.wireOp",EDGE,"E5");var subQ2=makeQuery(id+"F0.imprint","INTERSECT",VERTEX,{"derivedFrom":[subQ1,subQ0]});Q65=makeQuery(id+"F0.imprint","IMPRINT",FACE,{"disambiguationData":[TD([[makeQuery(id+"F0.imprint","IMPRINT",EDGE,{"disambiguationData":[TD([[subQ2,-1.0]])],"derivedFrom":subQ1}),-1.0]])]});}
            var Q66;
            {var subQ0=sQuery(id+"F0.wireOp",EDGE,"E20");Q66=makeQuery(id+"F0.imprint","IMPRINT",FACE,{"disambiguationData":[TD([[makeQuery(id+"F0.imprint","IMPRINT",EDGE,{"derivedFrom":subQ0}),-1.0]])]});}
            var Q67;
            {var subQ0=sQuery(id+"F0.wireOp",EDGE,"E54");var subQ1=sQuery(id+"F0.wireOp",EDGE,"E21");var subQ2=makeQuery(id+"F0.imprint","INTERSECT",VERTEX,{"derivedFrom":[subQ1,subQ0]});Q67=makeQuery(id+"F0.imprint","IMPRINT",FACE,{"disambiguationData":[TD([[makeQuery(id+"F0.imprint","IMPRINT",EDGE,{"disambiguationData":[TD([[subQ2,-1.0]])],"derivedFrom":subQ1}),1.0]])]});}
            var Q68;
            {var subQ0=sQuery(id+"F0.wireOp",EDGE,"E47");var subQ1=sQuery(id+"F0.wireOp",EDGE,"E9");var subQ2=makeQuery(id+"F0.imprint","INTERSECT",VERTEX,{"derivedFrom":[subQ1,subQ0]});Q68=makeQuery(id+"F0.imprint","IMPRINT",FACE,{"disambiguationData":[TD([[makeQuery(id+"F0.imprint","IMPRINT",EDGE,{"disambiguationData":[TD([[subQ2,-1.0]])],"derivedFrom":subQ1}),1.0]])]});}
            var Q69;
            {var subQ0=sQuery(id+"F0.wireOp",EDGE,"E10");Q69=makeQuery(id+"F0.imprint","IMPRINT",FACE,{"disambiguationData":[TD([[makeQuery(id+"F0.imprint","IMPRINT",EDGE,{"derivedFrom":subQ0}),1.0]])]});}
            var Q70;
            {var subQ0=sQuery(id+"F0.wireOp",EDGE,"E13");var subQ5=sQuery(id+"F0.wireOp",EDGE,"E47");var subQ6=makeQuery(id+"F0.imprint","INTERSECT",VERTEX,{"derivedFrom":[subQ0,subQ5]});Q70=makeQuery(id+"F0.imprint","IMPRINT",FACE,{"disambiguationData":[TD([[makeQuery(id+"F0.imprint","IMPRINT",EDGE,{"disambiguationData":[TD([[subQ6,-1.0]])],"derivedFrom":subQ5}),1.0]])]});}
            var Q71;
            {var subQ0=sQuery(id+"F0.wireOp",EDGE,"E7");var subQ1=sQuery(id+"F0.wireOp",EDGE,"E0.right");var subQ2=makeQuery(id+"F0.imprint","INTERSECT",VERTEX,{"derivedFrom":[subQ1,subQ0]});Q71=makeQuery(id+"F0.imprint","IMPRINT",FACE,{"disambiguationData":[TD([[makeQuery(id+"F0.imprint","IMPRINT",EDGE,{"disambiguationData":[TD([[subQ2,-1.0]])],"derivedFrom":subQ0}),-1.0]])]});}
            var Q72;
            {var subQ0=sQuery(id+"F0.wireOp",EDGE,"E54");var subQ1=sQuery(id+"F0.wireOp",EDGE,"E24");var subQ2=makeQuery(id+"F0.imprint","INTERSECT",VERTEX,{"derivedFrom":[subQ1,subQ0]});Q72=makeQuery(id+"F0.imprint","IMPRINT",FACE,{"disambiguationData":[TD([[makeQuery(id+"F0.imprint","IMPRINT",EDGE,{"disambiguationData":[TD([[subQ2,-1.0]])],"derivedFrom":subQ1}),-1.0]])]});}
            var Q73;
            {var subQ0=sQuery(id+"F0.wireOp",EDGE,"E49");var subQ1=sQuery(id+"F0.wireOp",EDGE,"E17");var subQ2=makeQuery(id+"F0.imprint","INTERSECT",VERTEX,{"derivedFrom":[subQ1,subQ0]});Q73=makeQuery(id+"F0.imprint","IMPRINT",FACE,{"disambiguationData":[TD([[makeQuery(id+"F0.imprint","IMPRINT",EDGE,{"disambiguationData":[TD([[subQ2,-1.0]])],"derivedFrom":subQ1}),1.0]])]});}
            var Q74;
            {var subQ0=sQuery(id+"F0.wireOp",EDGE,"E50");var subQ1=sQuery(id+"F0.wireOp",EDGE,"E15");var subQ2=makeQuery(id+"F0.imprint","INTERSECT",VERTEX,{"derivedFrom":[subQ1,subQ0]});Q74=makeQuery(id+"F0.imprint","IMPRINT",FACE,{"disambiguationData":[TD([[makeQuery(id+"F0.imprint","IMPRINT",EDGE,{"disambiguationData":[TD([[subQ2,-1.0]])],"derivedFrom":subQ1}),-1.0]])]});}
            var Q75;
            {var subQ0=sQuery(id+"F0.wireOp",EDGE,"E61");var subQ1=sQuery(id+"F0.wireOp",EDGE,"E11");var subQ2=makeQuery(id+"F0.imprint","INTERSECT",VERTEX,{"derivedFrom":[subQ1,subQ0]});Q75=makeQuery(id+"F0.imprint","IMPRINT",FACE,{"disambiguationData":[TD([[makeQuery(id+"F0.imprint","IMPRINT",EDGE,{"disambiguationData":[TD([[subQ2,-1.0]])],"derivedFrom":subQ1}),-1.0]])]});}
            var Q76;
            {var subQ0=sQuery(id+"F0.wireOp",EDGE,"E52");var subQ1=sQuery(id+"F0.wireOp",EDGE,"E5");var subQ2=makeQuery(id+"F0.imprint","INTERSECT",VERTEX,{"derivedFrom":[subQ1,subQ0]});Q76=makeQuery(id+"F0.imprint","IMPRINT",FACE,{"disambiguationData":[TD([[makeQuery(id+"F0.imprint","IMPRINT",EDGE,{"disambiguationData":[TD([[subQ2,-1.0]])],"derivedFrom":subQ1}),-1.0]])]});}
            var Q77;
            {var subQ0=sQuery(id+"F0.wireOp",EDGE,"E63");var subQ1=sQuery(id+"F0.wireOp",EDGE,"E15");var subQ2=makeQuery(id+"F0.imprint","INTERSECT",VERTEX,{"derivedFrom":[subQ1,subQ0]});Q77=makeQuery(id+"F0.imprint","IMPRINT",FACE,{"disambiguationData":[TD([[makeQuery(id+"F0.imprint","IMPRINT",EDGE,{"disambiguationData":[TD([[subQ2,-1.0]])],"derivedFrom":subQ1}),-1.0]])]});}
            var Q78;
            {var subQ0=sQuery(id+"F0.wireOp",EDGE,"E62");var subQ1=sQuery(id+"F0.wireOp",EDGE,"E9");var subQ2=makeQuery(id+"F0.imprint","INTERSECT",VERTEX,{"derivedFrom":[subQ1,subQ0]});Q78=makeQuery(id+"F0.imprint","IMPRINT",FACE,{"disambiguationData":[TD([[makeQuery(id+"F0.imprint","IMPRINT",EDGE,{"disambiguationData":[TD([[subQ2,-1.0]])],"derivedFrom":subQ1}),1.0]])]});}
            var Q79;
            {var subQ0=sQuery(id+"F0.wireOp",EDGE,"E53");var subQ1=sQuery(id+"F0.wireOp",EDGE,"E24");var subQ2=makeQuery(id+"F0.imprint","INTERSECT",VERTEX,{"derivedFrom":[subQ1,subQ0]});Q79=makeQuery(id+"F0.imprint","IMPRINT",FACE,{"disambiguationData":[TD([[makeQuery(id+"F0.imprint","IMPRINT",EDGE,{"disambiguationData":[TD([[subQ2,-1.0]])],"derivedFrom":subQ1}),-1.0]])]});}
            var Q80;
            {var subQ0=sQuery(id+"F0.wireOp",EDGE,"E50");var subQ1=sQuery(id+"F0.wireOp",EDGE,"E13");var subQ2=makeQuery(id+"F0.imprint","INTERSECT",VERTEX,{"derivedFrom":[subQ1,subQ0]});Q80=makeQuery(id+"F0.imprint","IMPRINT",FACE,{"disambiguationData":[TD([[makeQuery(id+"F0.imprint","IMPRINT",EDGE,{"disambiguationData":[TD([[subQ2,-1.0]])],"derivedFrom":subQ1}),1.0]])]});}
            var Q81;
            {var subQ0=sQuery(id+"F0.wireOp",EDGE,"E62");var subQ1=sQuery(id+"F0.wireOp",EDGE,"E11");var subQ2=makeQuery(id+"F0.imprint","INTERSECT",VERTEX,{"derivedFrom":[subQ1,subQ0]});Q81=makeQuery(id+"F0.imprint","IMPRINT",FACE,{"disambiguationData":[TD([[makeQuery(id+"F0.imprint","IMPRINT",EDGE,{"disambiguationData":[TD([[subQ2,-1.0]])],"derivedFrom":subQ1}),-1.0]])]});}
            var Q82;
            {var subQ0=sQuery(id+"F0.wireOp",EDGE,"E51");var subQ1=sQuery(id+"F0.wireOp",EDGE,"E3");var subQ2=makeQuery(id+"F0.imprint","INTERSECT",VERTEX,{"derivedFrom":[subQ1,subQ0]});Q82=makeQuery(id+"F0.imprint","IMPRINT",FACE,{"disambiguationData":[TD([[makeQuery(id+"F0.imprint","IMPRINT",EDGE,{"disambiguationData":[TD([[subQ2,-1.0]])],"derivedFrom":subQ1}),-1.0]])]});}
            var Q83;
            {var subQ1=sQuery(id+"F0.wireOp",EDGE,"E0.bottom");var subQ3=sQuery(id+"F0.wireOp",EDGE,"E47");var subQ4=makeQuery(id+"F0.imprint","INTERSECT",VERTEX,{"derivedFrom":[subQ1,subQ3]});Q83=makeQuery(id+"F0.imprint","IMPRINT",FACE,{"disambiguationData":[TD([[makeQuery(id+"F0.imprint","IMPRINT",EDGE,{"disambiguationData":[TD([[subQ4,-1.0]])],"derivedFrom":subQ3}),1.0]])]});}
            var Q84;
            {var subQ0=sQuery(id+"F0.wireOp",EDGE,"E64");var subQ1=sQuery(id+"F0.wireOp",EDGE,"E19");var subQ2=makeQuery(id+"F0.imprint","INTERSECT",VERTEX,{"derivedFrom":[subQ1,subQ0]});Q84=makeQuery(id+"F0.imprint","IMPRINT",FACE,{"disambiguationData":[TD([[makeQuery(id+"F0.imprint","IMPRINT",EDGE,{"disambiguationData":[TD([[subQ2,-1.0]])],"derivedFrom":subQ1}),-1.0]])]});}
            var Q85;
            {var subQ1=sQuery(id+"F0.wireOp",EDGE,"E1");var subQ5=sQuery(id+"F0.wireOp",EDGE,"E7");var subQ6=makeQuery(id+"F0.imprint","INTERSECT",VERTEX,{"derivedFrom":[subQ1,subQ5]});Q85=makeQuery(id+"F0.imprint","IMPRINT",FACE,{"disambiguationData":[TD([[makeQuery(id+"F0.imprint","IMPRINT",EDGE,{"disambiguationData":[TD([[subQ6,-1.0]])],"derivedFrom":subQ1}),-1.0]])]});}
            var Q86;
            {var subQ0=sQuery(id+"F0.wireOp",EDGE,"E53");var subQ1=sQuery(id+"F0.wireOp",EDGE,"E17");var subQ2=makeQuery(id+"F0.imprint","INTERSECT",VERTEX,{"derivedFrom":[subQ1,subQ0]});Q86=makeQuery(id+"F0.imprint","IMPRINT",FACE,{"disambiguationData":[TD([[makeQuery(id+"F0.imprint","IMPRINT",EDGE,{"disambiguationData":[TD([[subQ2,-1.0]])],"derivedFrom":subQ1}),1.0]])]});}
            var Q87;
            {var subQ0=sQuery(id+"F0.wireOp",EDGE,"E23");var subQ1=sQuery(id+"F0.wireOp",EDGE,"E1");var subQ2=makeQuery(id+"F0.imprint","INTERSECT",VERTEX,{"derivedFrom":[subQ1,subQ0]});Q87=makeQuery(id+"F0.imprint","IMPRINT",FACE,{"disambiguationData":[TD([[makeQuery(id+"F0.imprint","IMPRINT",EDGE,{"disambiguationData":[TD([[subQ2,-1.0]])],"derivedFrom":subQ1}),1.0]])]});}
            var Q88;
            {var subQ5=sQuery(id+"F0.wireOp",EDGE,"E61");var subQ7=sQuery(id+"F0.wireOp",EDGE,"E1");var subQ9=makeQuery(id+"F0.imprint","INTERSECT",VERTEX,{"derivedFrom":[subQ7,subQ5]});Q88=makeQuery(id+"F0.imprint","IMPRINT",FACE,{"disambiguationData":[TD([[makeQuery(id+"F0.imprint","IMPRINT",EDGE,{"disambiguationData":[TD([[subQ9,-1.0]])],"derivedFrom":subQ7}),1.0]])]});}
            var Q89;
            {var subQ0=sQuery(id+"F0.wireOp",EDGE,"E52");var subQ1=sQuery(id+"F0.wireOp",EDGE,"E4");var subQ2=makeQuery(id+"F0.imprint","INTERSECT",VERTEX,{"derivedFrom":[subQ1,subQ0]});Q89=makeQuery(id+"F0.imprint","IMPRINT",FACE,{"disambiguationData":[TD([[makeQuery(id+"F0.imprint","IMPRINT",EDGE,{"disambiguationData":[TD([[subQ2,-1.0]])],"derivedFrom":subQ1}),-1.0]])]});}
            var Q90;
            {var subQ1=sQuery(id+"F0.wireOp",EDGE,"E1");var subQ5=sQuery(id+"F0.wireOp",EDGE,"E21");var subQ6=makeQuery(id+"F0.imprint","INTERSECT",VERTEX,{"derivedFrom":[subQ1,subQ5]});Q90=makeQuery(id+"F0.imprint","IMPRINT",FACE,{"disambiguationData":[TD([[makeQuery(id+"F0.imprint","IMPRINT",EDGE,{"disambiguationData":[TD([[subQ6,-1.0]])],"derivedFrom":subQ1}),-1.0]])]});}
            var Q91;
            {var subQ0=sQuery(id+"F0.wireOp",EDGE,"E63");var subQ1=sQuery(id+"F0.wireOp",EDGE,"E23");var subQ2=makeQuery(id+"F0.imprint","INTERSECT",VERTEX,{"derivedFrom":[subQ1,subQ0]});Q91=makeQuery(id+"F0.imprint","IMPRINT",FACE,{"disambiguationData":[TD([[makeQuery(id+"F0.imprint","IMPRINT",EDGE,{"disambiguationData":[TD([[subQ2,-1.0]])],"derivedFrom":subQ1}),-1.0]])]});}
            var Q92;
            {var subQ5=sQuery(id+"F0.wireOp",EDGE,"E23");var subQ6=sQuery(id+"F0.wireOp",EDGE,"E1");var subQ7=makeQuery(id+"F0.imprint","INTERSECT",VERTEX,{"derivedFrom":[subQ6,subQ5]});Q92=makeQuery(id+"F0.imprint","IMPRINT",FACE,{"disambiguationData":[TD([[makeQuery(id+"F0.imprint","IMPRINT",EDGE,{"disambiguationData":[TD([[subQ7,-1.0]])],"derivedFrom":subQ6}),-1.0]])]});}
            var Q93;
            {var subQ0=sQuery(id+"F0.wireOp",EDGE,"E62");var subQ1=sQuery(id+"F0.wireOp",EDGE,"E19");var subQ2=makeQuery(id+"F0.imprint","INTERSECT",VERTEX,{"derivedFrom":[subQ1,subQ0]});Q93=makeQuery(id+"F0.imprint","IMPRINT",FACE,{"disambiguationData":[TD([[makeQuery(id+"F0.imprint","IMPRINT",EDGE,{"disambiguationData":[TD([[subQ2,-1.0]])],"derivedFrom":subQ1}),-1.0]])]});}
            var Q94;
            {var subQ0=sQuery(id+"F0.wireOp",EDGE,"E50");var subQ1=sQuery(id+"F0.wireOp",EDGE,"E6");var subQ2=makeQuery(id+"F0.imprint","INTERSECT",VERTEX,{"derivedFrom":[subQ1,subQ0]});Q94=makeQuery(id+"F0.imprint","IMPRINT",FACE,{"disambiguationData":[TD([[makeQuery(id+"F0.imprint","IMPRINT",EDGE,{"disambiguationData":[TD([[subQ2,-1.0]])],"derivedFrom":subQ1}),-1.0]])]});}
            var Q95;
            {var subQ0=sQuery(id+"F0.wireOp",EDGE,"E54");var subQ1=sQuery(id+"F0.wireOp",EDGE,"E4");var subQ2=makeQuery(id+"F0.imprint","INTERSECT",VERTEX,{"derivedFrom":[subQ1,subQ0]});Q95=makeQuery(id+"F0.imprint","IMPRINT",FACE,{"disambiguationData":[TD([[makeQuery(id+"F0.imprint","IMPRINT",EDGE,{"disambiguationData":[TD([[subQ2,-1.0]])],"derivedFrom":subQ1}),-1.0]])]});}
            var Q96;
            {var subQ0=sQuery(id+"F0.wireOp",EDGE,"E7");var subQ1=sQuery(id+"F0.wireOp",EDGE,"E2");var subQ2=makeQuery(id+"F0.imprint","INTERSECT",VERTEX,{"derivedFrom":[subQ1,subQ0]});Q96=makeQuery(id+"F0.imprint","IMPRINT",FACE,{"disambiguationData":[TD([[makeQuery(id+"F0.imprint","IMPRINT",EDGE,{"disambiguationData":[TD([[subQ2,-1.0]])],"derivedFrom":subQ1}),1.0]])]});}
            var Q97;
            {var subQ0=sQuery(id+"F0.wireOp",EDGE,"E21");var subQ1=sQuery(id+"F0.wireOp",EDGE,"E2");var subQ2=makeQuery(id+"F0.imprint","INTERSECT",VERTEX,{"derivedFrom":[subQ1,subQ0]});Q97=makeQuery(id+"F0.imprint","IMPRINT",FACE,{"disambiguationData":[TD([[makeQuery(id+"F0.imprint","IMPRINT",EDGE,{"disambiguationData":[TD([[subQ2,-1.0]])],"derivedFrom":subQ1}),1.0]])]});}
            var Q98;
            {var subQ0=sQuery(id+"F0.wireOp",EDGE,"E52");var subQ1=sQuery(id+"F0.wireOp",EDGE,"E23");var subQ2=makeQuery(id+"F0.imprint","INTERSECT",VERTEX,{"derivedFrom":[subQ1,subQ0]});Q98=makeQuery(id+"F0.imprint","IMPRINT",FACE,{"disambiguationData":[TD([[makeQuery(id+"F0.imprint","IMPRINT",EDGE,{"disambiguationData":[TD([[subQ2,-1.0]])],"derivedFrom":subQ1}),-1.0]])]});}
            var Q99;
            {var subQ0=sQuery(id+"F0.wireOp",EDGE,"E50");var subQ1=sQuery(id+"F0.wireOp",EDGE,"E3");var subQ2=makeQuery(id+"F0.imprint","INTERSECT",VERTEX,{"derivedFrom":[subQ1,subQ0]});Q99=makeQuery(id+"F0.imprint","IMPRINT",FACE,{"disambiguationData":[TD([[makeQuery(id+"F0.imprint","IMPRINT",EDGE,{"disambiguationData":[TD([[subQ2,-1.0]])],"derivedFrom":subQ1}),-1.0]])]});}
            var Q100;
            {var subQ5=sQuery(id+"F0.wireOp",EDGE,"E13");var subQ6=sQuery(id+"F0.wireOp",EDGE,"E1");var subQ7=makeQuery(id+"F0.imprint","INTERSECT",VERTEX,{"derivedFrom":[subQ6,subQ5]});Q100=makeQuery(id+"F0.imprint","IMPRINT",FACE,{"disambiguationData":[TD([[makeQuery(id+"F0.imprint","IMPRINT",EDGE,{"disambiguationData":[TD([[subQ7,-1.0]])],"derivedFrom":subQ6}),-1.0]])]});}
            var Q101;
            {var subQ1=sQuery(id+"F0.wireOp",EDGE,"E2");var subQ5=sQuery(id+"F0.wireOp",EDGE,"E17");var subQ6=makeQuery(id+"F0.imprint","INTERSECT",VERTEX,{"derivedFrom":[subQ1,subQ5]});Q101=makeQuery(id+"F0.imprint","IMPRINT",FACE,{"disambiguationData":[TD([[makeQuery(id+"F0.imprint","IMPRINT",EDGE,{"disambiguationData":[TD([[subQ6,-1.0]])],"derivedFrom":subQ1}),1.0]])]});}
            var Q102;
            {var subQ0=sQuery(id+"F0.wireOp",EDGE,"E3");var subQ1=sQuery(id+"F0.wireOp",EDGE,"E0.left");var subQ2=makeQuery(id+"F0.imprint","INTERSECT",VERTEX,{"derivedFrom":[subQ1,subQ0]});Q102=makeQuery(id+"F0.imprint","IMPRINT",FACE,{"disambiguationData":[TD([[makeQuery(id+"F0.imprint","IMPRINT",EDGE,{"disambiguationData":[TD([[subQ2,-1.0]])],"derivedFrom":subQ1}),-1.0]])]});}
            var Q103;
            {var subQ5=sQuery(id+"F0.wireOp",EDGE,"E5");var subQ7=sQuery(id+"F0.wireOp",EDGE,"E1");var subQ8=makeQuery(id+"F0.imprint","INTERSECT",VERTEX,{"derivedFrom":[subQ7,subQ5]});Q103=makeQuery(id+"F0.imprint","IMPRINT",FACE,{"disambiguationData":[TD([[makeQuery(id+"F0.imprint","IMPRINT",EDGE,{"disambiguationData":[TD([[subQ8,-1.0]])],"derivedFrom":subQ7}),-1.0]])]});}
            var Q104;
            {var subQ5=sQuery(id+"F0.wireOp",EDGE,"E1");var subQ7=sQuery(id+"F0.wireOp",EDGE,"E52");var subQ9=makeQuery(id+"F0.imprint","INTERSECT",VERTEX,{"derivedFrom":[subQ5,subQ7]});Q104=makeQuery(id+"F0.imprint","IMPRINT",FACE,{"disambiguationData":[TD([[makeQuery(id+"F0.imprint","IMPRINT",EDGE,{"disambiguationData":[TD([[subQ9,-1.0]])],"derivedFrom":subQ5}),1.0]])]});}
            var Q105;
            {var subQ0=sQuery(id+"F0.wireOp",EDGE,"E52");var subQ1=sQuery(id+"F0.wireOp",EDGE,"E3");var subQ2=makeQuery(id+"F0.imprint","INTERSECT",VERTEX,{"derivedFrom":[subQ1,subQ0]});Q105=makeQuery(id+"F0.imprint","IMPRINT",FACE,{"disambiguationData":[TD([[makeQuery(id+"F0.imprint","IMPRINT",EDGE,{"disambiguationData":[TD([[subQ2,-1.0]])],"derivedFrom":subQ1}),-1.0]])]});}
            var Q106;
            {var subQ0=sQuery(id+"F0.wireOp",EDGE,"E48");var subQ1=sQuery(id+"F0.wireOp",EDGE,"E19");var subQ2=makeQuery(id+"F0.imprint","INTERSECT",VERTEX,{"derivedFrom":[subQ1,subQ0]});Q106=makeQuery(id+"F0.imprint","IMPRINT",FACE,{"disambiguationData":[TD([[makeQuery(id+"F0.imprint","IMPRINT",EDGE,{"disambiguationData":[TD([[subQ2,-1.0]])],"derivedFrom":subQ1}),-1.0]])]});}
            var Q107;
            {var subQ0=sQuery(id+"F0.wireOp",EDGE,"E49");var subQ1=sQuery(id+"F0.wireOp",EDGE,"E13");var subQ2=makeQuery(id+"F0.imprint","INTERSECT",VERTEX,{"derivedFrom":[subQ1,subQ0]});Q107=makeQuery(id+"F0.imprint","IMPRINT",FACE,{"disambiguationData":[TD([[makeQuery(id+"F0.imprint","IMPRINT",EDGE,{"disambiguationData":[TD([[subQ2,-1.0]])],"derivedFrom":subQ1}),1.0]])]});}
            var Q108;
            {var subQ0=sQuery(id+"F0.wireOp",EDGE,"E28");Q108=makeQuery(id+"F0.imprint","IMPRINT",FACE,{"disambiguationData":[TD([[makeQuery(id+"F0.imprint","IMPRINT",EDGE,{"derivedFrom":subQ0}),-1.0]])]});}
            var Q109;
            {var subQ0=sQuery(id+"F0.wireOp",EDGE,"E15");var subQ5=sQuery(id+"F0.wireOp",EDGE,"E64");var subQ6=makeQuery(id+"F0.imprint","INTERSECT",VERTEX,{"derivedFrom":[subQ0,subQ5]});Q109=makeQuery(id+"F0.imprint","IMPRINT",FACE,{"disambiguationData":[TD([[makeQuery(id+"F0.imprint","IMPRINT",EDGE,{"disambiguationData":[TD([[subQ6,-1.0]])],"derivedFrom":subQ5}),-1.0]])]});}
            var Q110;
            {var subQ0=sQuery(id+"F0.wireOp",EDGE,"E55");var subQ1=sQuery(id+"F0.wireOp",EDGE,"E5");var subQ2=makeQuery(id+"F0.imprint","INTERSECT",VERTEX,{"derivedFrom":[subQ1,subQ0]});Q110=makeQuery(id+"F0.imprint","IMPRINT",FACE,{"disambiguationData":[TD([[makeQuery(id+"F0.imprint","IMPRINT",EDGE,{"disambiguationData":[TD([[subQ2,-1.0]])],"derivedFrom":subQ1}),-1.0]])]});}
            var Q111;
            {var subQ5=sQuery(id+"F0.wireOp",EDGE,"E2");var subQ7=sQuery(id+"F0.wireOp",EDGE,"E55");var subQ9=makeQuery(id+"F0.imprint","INTERSECT",VERTEX,{"derivedFrom":[subQ5,subQ7]});Q111=makeQuery(id+"F0.imprint","IMPRINT",FACE,{"disambiguationData":[TD([[makeQuery(id+"F0.imprint","IMPRINT",EDGE,{"disambiguationData":[TD([[subQ9,-1.0]])],"derivedFrom":subQ5}),-1.0]])]});}
            var Q112;
            {var subQ5=sQuery(id+"F0.wireOp",EDGE,"E49");var subQ7=sQuery(id+"F0.wireOp",EDGE,"E2");var subQ9=makeQuery(id+"F0.imprint","INTERSECT",VERTEX,{"derivedFrom":[subQ7,subQ5]});Q112=makeQuery(id+"F0.imprint","IMPRINT",FACE,{"disambiguationData":[TD([[makeQuery(id+"F0.imprint","IMPRINT",EDGE,{"disambiguationData":[TD([[subQ9,-1.0]])],"derivedFrom":subQ7}),-1.0]])]});}
            var Q113;
            {var subQ0=sQuery(id+"F0.wireOp",EDGE,"E3");var subQ1=sQuery(id+"F0.wireOp",EDGE,"E1");var subQ2=makeQuery(id+"F0.imprint","INTERSECT",VERTEX,{"derivedFrom":[subQ1,subQ0]});Q113=makeQuery(id+"F0.imprint","IMPRINT",FACE,{"disambiguationData":[TD([[makeQuery(id+"F0.imprint","IMPRINT",EDGE,{"disambiguationData":[TD([[subQ2,-1.0]])],"derivedFrom":subQ1}),1.0]])]});}
            var Q114;
            {var subQ0=sQuery(id+"F0.wireOp",EDGE,"E63");var subQ1=sQuery(id+"F0.wireOp",EDGE,"E17");var subQ2=makeQuery(id+"F0.imprint","INTERSECT",VERTEX,{"derivedFrom":[subQ1,subQ0]});Q114=makeQuery(id+"F0.imprint","IMPRINT",FACE,{"disambiguationData":[TD([[makeQuery(id+"F0.imprint","IMPRINT",EDGE,{"disambiguationData":[TD([[subQ2,-1.0]])],"derivedFrom":subQ1}),1.0]])]});}
            var Q115;
            {var subQ1=sQuery(id+"F0.wireOp",EDGE,"E1");var subQ5=sQuery(id+"F0.wireOp",EDGE,"E60");var subQ9=makeQuery(id+"F0.imprint","INTERSECT",VERTEX,{"derivedFrom":[subQ1,subQ5]});Q115=makeQuery(id+"F0.imprint","IMPRINT",FACE,{"disambiguationData":[TD([[makeQuery(id+"F0.imprint","IMPRINT",EDGE,{"disambiguationData":[TD([[subQ9,-1.0]])],"derivedFrom":subQ1}),1.0]])]});}
            var Q116;
            {var subQ0=sQuery(id+"F0.wireOp",EDGE,"E55");var subQ1=sQuery(id+"F0.wireOp",EDGE,"E3");var subQ2=makeQuery(id+"F0.imprint","INTERSECT",VERTEX,{"derivedFrom":[subQ1,subQ0]});Q116=makeQuery(id+"F0.imprint","IMPRINT",FACE,{"disambiguationData":[TD([[makeQuery(id+"F0.imprint","IMPRINT",EDGE,{"disambiguationData":[TD([[subQ2,-1.0]])],"derivedFrom":subQ1}),-1.0]])]});}
            var Q117;
            {var subQ5=sQuery(id+"F0.wireOp",EDGE,"E2");var subQ7=sQuery(id+"F0.wireOp",EDGE,"E52");var subQ9=makeQuery(id+"F0.imprint","INTERSECT",VERTEX,{"derivedFrom":[subQ5,subQ7]});Q117=makeQuery(id+"F0.imprint","IMPRINT",FACE,{"disambiguationData":[TD([[makeQuery(id+"F0.imprint","IMPRINT",EDGE,{"disambiguationData":[TD([[subQ9,-1.0]])],"derivedFrom":subQ5}),-1.0]])]});}
            var Q118;
            {var subQ1=sQuery(id+"F0.wireOp",EDGE,"E35");Q118=makeQuery(id+"F0.imprint","IMPRINT",FACE,{"disambiguationData":[TD([[makeQuery(id+"F0.imprint","IMPRINT",EDGE,{"derivedFrom":subQ1}),-1.0]])]});}
            var Q119;
            {var subQ0=sQuery(id+"F0.wireOp",EDGE,"E50");var subQ7=sQuery(id+"F0.wireOp",EDGE,"E2");var subQ9=makeQuery(id+"F0.imprint","INTERSECT",VERTEX,{"derivedFrom":[subQ7,subQ0]});Q119=makeQuery(id+"F0.imprint","IMPRINT",FACE,{"disambiguationData":[TD([[makeQuery(id+"F0.imprint","IMPRINT",EDGE,{"disambiguationData":[TD([[subQ9,-1.0]])],"derivedFrom":subQ7}),-1.0]])]});}
            var Q120;
            {var subQ0=sQuery(id+"F0.wireOp",EDGE,"E55");var subQ1=sQuery(id+"F0.wireOp",EDGE,"E21");var subQ2=makeQuery(id+"F0.imprint","INTERSECT",VERTEX,{"derivedFrom":[subQ1,subQ0]});Q120=makeQuery(id+"F0.imprint","IMPRINT",FACE,{"disambiguationData":[TD([[makeQuery(id+"F0.imprint","IMPRINT",EDGE,{"disambiguationData":[TD([[subQ2,-1.0]])],"derivedFrom":subQ1}),1.0]])]});}
            var Q121;
            {var subQ0=sQuery(id+"F0.wireOp",EDGE,"E55");var subQ1=sQuery(id+"F0.wireOp",EDGE,"E7");var subQ2=makeQuery(id+"F0.imprint","INTERSECT",VERTEX,{"derivedFrom":[subQ1,subQ0]});Q121=makeQuery(id+"F0.imprint","IMPRINT",FACE,{"disambiguationData":[TD([[makeQuery(id+"F0.imprint","IMPRINT",EDGE,{"disambiguationData":[TD([[subQ2,-1.0]])],"derivedFrom":subQ1}),-1.0]])]});}
            var Q122;
            {var subQ0=sQuery(id+"F0.wireOp",EDGE,"E61");var subQ1=sQuery(id+"F0.wireOp",EDGE,"E13");var subQ2=makeQuery(id+"F0.imprint","INTERSECT",VERTEX,{"derivedFrom":[subQ1,subQ0]});Q122=makeQuery(id+"F0.imprint","IMPRINT",FACE,{"disambiguationData":[TD([[makeQuery(id+"F0.imprint","IMPRINT",EDGE,{"disambiguationData":[TD([[subQ2,-1.0]])],"derivedFrom":subQ1}),1.0]])]});}
            var Q123;
            {var subQ1=sQuery(id+"F0.wireOp",EDGE,"E0.left");var subQ3=sQuery(id+"F0.wireOp",EDGE,"E3");var subQ4=makeQuery(id+"F0.imprint","INTERSECT",VERTEX,{"derivedFrom":[subQ1,subQ3]});Q123=makeQuery(id+"F0.imprint","IMPRINT",FACE,{"disambiguationData":[TD([[makeQuery(id+"F0.imprint","IMPRINT",EDGE,{"disambiguationData":[TD([[subQ4,1.0]])],"derivedFrom":subQ3}),1.0]])]});}
            var Q124;
            {var subQ0=sQuery(id+"F0.wireOp",EDGE,"E5");var subQ1=sQuery(id+"F0.wireOp",EDGE,"E0.right");var subQ2=makeQuery(id+"F0.imprint","INTERSECT",VERTEX,{"derivedFrom":[subQ1,subQ0]});Q124=makeQuery(id+"F0.imprint","IMPRINT",FACE,{"disambiguationData":[TD([[makeQuery(id+"F0.imprint","IMPRINT",EDGE,{"disambiguationData":[TD([[subQ2,-1.0]])],"derivedFrom":subQ1}),1.0]])]});}
            var Q125;
            {var subQ0=sQuery(id+"F0.wireOp",EDGE,"E61");var subQ1=sQuery(id+"F0.wireOp",EDGE,"E4");var subQ2=makeQuery(id+"F0.imprint","INTERSECT",VERTEX,{"derivedFrom":[subQ1,subQ0]});Q125=makeQuery(id+"F0.imprint","IMPRINT",FACE,{"disambiguationData":[TD([[makeQuery(id+"F0.imprint","IMPRINT",EDGE,{"disambiguationData":[TD([[subQ2,-1.0]])],"derivedFrom":subQ1}),-1.0]])]});}
            var Q126;
            {var subQ0=sQuery(id+"F0.wireOp",EDGE,"E21");var subQ1=sQuery(id+"F0.wireOp",EDGE,"E2");var subQ2=makeQuery(id+"F0.imprint","INTERSECT",VERTEX,{"derivedFrom":[subQ1,subQ0]});Q126=makeQuery(id+"F0.imprint","IMPRINT",FACE,{"disambiguationData":[TD([[makeQuery(id+"F0.imprint","IMPRINT",EDGE,{"disambiguationData":[TD([[subQ2,-1.0]])],"derivedFrom":subQ1}),-1.0]])]});}
            var Q127;
            {var subQ5=sQuery(id+"F0.wireOp",EDGE,"E1");var subQ7=sQuery(id+"F0.wireOp",EDGE,"E9");var subQ9=makeQuery(id+"F0.imprint","INTERSECT",VERTEX,{"derivedFrom":[subQ5,subQ7]});Q127=makeQuery(id+"F0.imprint","IMPRINT",FACE,{"disambiguationData":[TD([[makeQuery(id+"F0.imprint","IMPRINT",EDGE,{"disambiguationData":[TD([[subQ9,-1.0]])],"derivedFrom":subQ5}),-1.0]])]});}
            var Q128;
            {var subQ0=sQuery(id+"F0.wireOp",EDGE,"E48");var subQ1=sQuery(id+"F0.wireOp",EDGE,"E15");var subQ2=makeQuery(id+"F0.imprint","INTERSECT",VERTEX,{"derivedFrom":[subQ1,subQ0]});Q128=makeQuery(id+"F0.imprint","IMPRINT",FACE,{"disambiguationData":[TD([[makeQuery(id+"F0.imprint","IMPRINT",EDGE,{"disambiguationData":[TD([[subQ2,-1.0]])],"derivedFrom":subQ1}),-1.0]])]});}
            var Q129;
            {var subQ0=sQuery(id+"F0.wireOp",EDGE,"E51");var subQ1=sQuery(id+"F0.wireOp",EDGE,"E9");var subQ2=makeQuery(id+"F0.imprint","INTERSECT",VERTEX,{"derivedFrom":[subQ1,subQ0]});Q129=makeQuery(id+"F0.imprint","IMPRINT",FACE,{"disambiguationData":[TD([[makeQuery(id+"F0.imprint","IMPRINT",EDGE,{"disambiguationData":[TD([[subQ2,-1.0]])],"derivedFrom":subQ1}),1.0]])]});}
            var Q130;
            {var subQ0=sQuery(id+"F0.wireOp",EDGE,"E57");Q130=makeQuery(id+"F0.imprint","IMPRINT",FACE,{"disambiguationData":[TD([[makeQuery(id+"F0.imprint","IMPRINT",EDGE,{"derivedFrom":subQ0}),-1.0]])]});}
            var Q131;
            {var subQ0=sQuery(id+"F0.wireOp",EDGE,"E19");var subQ5=sQuery(id+"F0.wireOp",EDGE,"E64");var subQ6=makeQuery(id+"F0.imprint","INTERSECT",VERTEX,{"derivedFrom":[subQ0,subQ5]});Q131=makeQuery(id+"F0.imprint","IMPRINT",FACE,{"disambiguationData":[TD([[makeQuery(id+"F0.imprint","IMPRINT",EDGE,{"disambiguationData":[TD([[subQ6,-1.0]])],"derivedFrom":subQ5}),-1.0]])]});}
            var Q132;
            {var subQ0=sQuery(id+"F0.wireOp",EDGE,"E62");var subQ1=sQuery(id+"F0.wireOp",EDGE,"E4");var subQ2=makeQuery(id+"F0.imprint","INTERSECT",VERTEX,{"derivedFrom":[subQ1,subQ0]});Q132=makeQuery(id+"F0.imprint","IMPRINT",FACE,{"disambiguationData":[TD([[makeQuery(id+"F0.imprint","IMPRINT",EDGE,{"disambiguationData":[TD([[subQ2,-1.0]])],"derivedFrom":subQ1}),-1.0]])]});}
            var Q133;
            {var subQ1=sQuery(id+"F0.wireOp",EDGE,"E2");var subQ5=sQuery(id+"F0.wireOp",EDGE,"E4");var subQ6=makeQuery(id+"F0.imprint","INTERSECT",VERTEX,{"derivedFrom":[subQ1,subQ5]});Q133=makeQuery(id+"F0.imprint","IMPRINT",FACE,{"disambiguationData":[TD([[makeQuery(id+"F0.imprint","IMPRINT",EDGE,{"disambiguationData":[TD([[subQ6,-1.0]])],"derivedFrom":subQ1}),1.0]])]});}
            var Q134;
            {var subQ0=sQuery(id+"F0.wireOp",EDGE,"E19");var subQ1=sQuery(id+"F0.wireOp",EDGE,"E2");var subQ2=makeQuery(id+"F0.imprint","INTERSECT",VERTEX,{"derivedFrom":[subQ1,subQ0]});Q134=makeQuery(id+"F0.imprint","IMPRINT",FACE,{"disambiguationData":[TD([[makeQuery(id+"F0.imprint","IMPRINT",EDGE,{"disambiguationData":[TD([[subQ2,-1.0]])],"derivedFrom":subQ1}),1.0]])]});}
            var Q135;
            {var subQ0=sQuery(id+"F0.wireOp",EDGE,"E16");Q135=makeQuery(id+"F0.imprint","IMPRINT",FACE,{"disambiguationData":[TD([[makeQuery(id+"F0.imprint","IMPRINT",EDGE,{"derivedFrom":subQ0}),-1.0]])]});}
            var Q136;
            {var subQ0=sQuery(id+"F0.wireOp",EDGE,"E7");var subQ1=sQuery(id+"F0.wireOp",EDGE,"E2");var subQ2=makeQuery(id+"F0.imprint","INTERSECT",VERTEX,{"derivedFrom":[subQ1,subQ0]});Q136=makeQuery(id+"F0.imprint","IMPRINT",FACE,{"disambiguationData":[TD([[makeQuery(id+"F0.imprint","IMPRINT",EDGE,{"disambiguationData":[TD([[subQ2,-1.0]])],"derivedFrom":subQ1}),-1.0]])]});}
            var Q137;
            {var subQ1=sQuery(id+"F0.wireOp",EDGE,"E2");var subQ7=sQuery(id+"F0.wireOp",EDGE,"E15");var subQ9=makeQuery(id+"F0.imprint","INTERSECT",VERTEX,{"derivedFrom":[subQ1,subQ7]});Q137=makeQuery(id+"F0.imprint","IMPRINT",FACE,{"disambiguationData":[TD([[makeQuery(id+"F0.imprint","IMPRINT",EDGE,{"disambiguationData":[TD([[subQ9,-1.0]])],"derivedFrom":subQ1}),1.0]])]});}
            var Q138;
            {var subQ0=sQuery(id+"F0.wireOp",EDGE,"E48");var subQ1=sQuery(id+"F0.wireOp",EDGE,"E4");var subQ2=makeQuery(id+"F0.imprint","INTERSECT",VERTEX,{"derivedFrom":[subQ1,subQ0]});Q138=makeQuery(id+"F0.imprint","IMPRINT",FACE,{"disambiguationData":[TD([[makeQuery(id+"F0.imprint","IMPRINT",EDGE,{"disambiguationData":[TD([[subQ2,-1.0]])],"derivedFrom":subQ1}),-1.0]])]});}
            var Q139;
            {var subQ0=sQuery(id+"F0.wireOp",EDGE,"E49");var subQ1=sQuery(id+"F0.wireOp",EDGE,"E19");var subQ2=makeQuery(id+"F0.imprint","INTERSECT",VERTEX,{"derivedFrom":[subQ1,subQ0]});Q139=makeQuery(id+"F0.imprint","IMPRINT",FACE,{"disambiguationData":[TD([[makeQuery(id+"F0.imprint","IMPRINT",EDGE,{"disambiguationData":[TD([[subQ2,-1.0]])],"derivedFrom":subQ1}),-1.0]])]});}
            var Q140;
            {var subQ0=sQuery(id+"F0.wireOp",EDGE,"E49");var subQ1=sQuery(id+"F0.wireOp",EDGE,"E6");var subQ2=makeQuery(id+"F0.imprint","INTERSECT",VERTEX,{"derivedFrom":[subQ1,subQ0]});Q140=makeQuery(id+"F0.imprint","IMPRINT",FACE,{"disambiguationData":[TD([[makeQuery(id+"F0.imprint","IMPRINT",EDGE,{"disambiguationData":[TD([[subQ2,-1.0]])],"derivedFrom":subQ1}),-1.0]])]});}
            var Q141;
            {var subQ0=sQuery(id+"F0.wireOp",EDGE,"E54");var subQ1=sQuery(id+"F0.wireOp",EDGE,"E3");var subQ2=makeQuery(id+"F0.imprint","INTERSECT",VERTEX,{"derivedFrom":[subQ1,subQ0]});Q141=makeQuery(id+"F0.imprint","IMPRINT",FACE,{"disambiguationData":[TD([[makeQuery(id+"F0.imprint","IMPRINT",EDGE,{"disambiguationData":[TD([[subQ2,-1.0]])],"derivedFrom":subQ1}),1.0]])]});}
            var Q142;
            {var subQ0=sQuery(id+"F0.wireOp",EDGE,"E53");var subQ1=sQuery(id+"F0.wireOp",EDGE,"E3");var subQ2=makeQuery(id+"F0.imprint","INTERSECT",VERTEX,{"derivedFrom":[subQ1,subQ0]});Q142=makeQuery(id+"F0.imprint","IMPRINT",FACE,{"disambiguationData":[TD([[makeQuery(id+"F0.imprint","IMPRINT",EDGE,{"disambiguationData":[TD([[subQ2,-1.0]])],"derivedFrom":subQ1}),1.0]])]});}
            var Q143;
            {var subQ0=sQuery(id+"F0.wireOp",EDGE,"E62");var subQ1=sQuery(id+"F0.wireOp",EDGE,"E23");var subQ2=makeQuery(id+"F0.imprint","INTERSECT",VERTEX,{"derivedFrom":[subQ1,subQ0]});Q143=makeQuery(id+"F0.imprint","IMPRINT",FACE,{"disambiguationData":[TD([[makeQuery(id+"F0.imprint","IMPRINT",EDGE,{"disambiguationData":[TD([[subQ2,-1.0]])],"derivedFrom":subQ1}),-1.0]])]});}
            var Q144;
            {var subQ0=sQuery(id+"F0.wireOp",EDGE,"E48");var subQ1=sQuery(id+"F0.wireOp",EDGE,"E2");var subQ2=makeQuery(id+"F0.imprint","INTERSECT",VERTEX,{"derivedFrom":[subQ1,subQ0]});Q144=makeQuery(id+"F0.imprint","IMPRINT",FACE,{"disambiguationData":[TD([[makeQuery(id+"F0.imprint","IMPRINT",EDGE,{"disambiguationData":[TD([[subQ2,-1.0]])],"derivedFrom":subQ1}),1.0]])]});}
            var Q145;
            {var subQ0=sQuery(id+"F0.wireOp",EDGE,"E62");var subQ1=sQuery(id+"F0.wireOp",EDGE,"E15");var subQ2=makeQuery(id+"F0.imprint","INTERSECT",VERTEX,{"derivedFrom":[subQ1,subQ0]});Q145=makeQuery(id+"F0.imprint","IMPRINT",FACE,{"disambiguationData":[TD([[makeQuery(id+"F0.imprint","IMPRINT",EDGE,{"disambiguationData":[TD([[subQ2,-1.0]])],"derivedFrom":subQ1}),-1.0]])]});}
            var Q146;
            {var subQ0=sQuery(id+"F0.wireOp",EDGE,"E54");var subQ1=sQuery(id+"F0.wireOp",EDGE,"E3");var subQ2=makeQuery(id+"F0.imprint","INTERSECT",VERTEX,{"derivedFrom":[subQ1,subQ0]});Q146=makeQuery(id+"F0.imprint","IMPRINT",FACE,{"disambiguationData":[TD([[makeQuery(id+"F0.imprint","IMPRINT",EDGE,{"disambiguationData":[TD([[subQ2,-1.0]])],"derivedFrom":subQ1}),-1.0]])]});}
            var Q147;
            {var subQ0=sQuery(id+"F0.wireOp",EDGE,"E47");var subQ1=sQuery(id+"F0.wireOp",EDGE,"E17");var subQ2=makeQuery(id+"F0.imprint","INTERSECT",VERTEX,{"derivedFrom":[subQ1,subQ0]});Q147=makeQuery(id+"F0.imprint","IMPRINT",FACE,{"disambiguationData":[TD([[makeQuery(id+"F0.imprint","IMPRINT",EDGE,{"disambiguationData":[TD([[subQ2,-1.0]])],"derivedFrom":subQ1}),1.0]])]});}
            var Q148;
            {var subQ0=sQuery(id+"F0.wireOp",EDGE,"E50");var subQ1=sQuery(id+"F0.wireOp",EDGE,"E9");var subQ2=makeQuery(id+"F0.imprint","INTERSECT",VERTEX,{"derivedFrom":[subQ1,subQ0]});Q148=makeQuery(id+"F0.imprint","IMPRINT",FACE,{"disambiguationData":[TD([[makeQuery(id+"F0.imprint","IMPRINT",EDGE,{"disambiguationData":[TD([[subQ2,-1.0]])],"derivedFrom":subQ1}),1.0]])]});}
            var Q149;
            {var subQ5=sQuery(id+"F0.wireOp",EDGE,"E1");var subQ7=sQuery(id+"F0.wireOp",EDGE,"E48");var subQ9=makeQuery(id+"F0.imprint","INTERSECT",VERTEX,{"derivedFrom":[subQ5,subQ7]});Q149=makeQuery(id+"F0.imprint","IMPRINT",FACE,{"disambiguationData":[TD([[makeQuery(id+"F0.imprint","IMPRINT",EDGE,{"disambiguationData":[TD([[subQ9,-1.0]])],"derivedFrom":subQ5}),1.0]])]});}
            var Q150;
            {var subQ1=sQuery(id+"F0.wireOp",EDGE,"E2");var subQ7=sQuery(id+"F0.wireOp",EDGE,"E9");var subQ8=makeQuery(id+"F0.imprint","INTERSECT",VERTEX,{"derivedFrom":[subQ1,subQ7]});Q150=makeQuery(id+"F0.imprint","IMPRINT",FACE,{"disambiguationData":[TD([[makeQuery(id+"F0.imprint","IMPRINT",EDGE,{"disambiguationData":[TD([[subQ8,-1.0]])],"derivedFrom":subQ1}),1.0]])]});}
            var Q151;
            {var subQ0=sQuery(id+"F0.wireOp",EDGE,"E48");var subQ1=sQuery(id+"F0.wireOp",EDGE,"E13");var subQ2=makeQuery(id+"F0.imprint","INTERSECT",VERTEX,{"derivedFrom":[subQ1,subQ0]});Q151=makeQuery(id+"F0.imprint","IMPRINT",FACE,{"disambiguationData":[TD([[makeQuery(id+"F0.imprint","IMPRINT",EDGE,{"disambiguationData":[TD([[subQ2,-1.0]])],"derivedFrom":subQ1}),1.0]])]});}
            var Q152;
            {var subQ5=sQuery(id+"F0.wireOp",EDGE,"E56");Q152=makeQuery(id+"F0.imprint","IMPRINT",FACE,{"disambiguationData":[TD([[makeQuery(id+"F0.imprint","IMPRINT",EDGE,{"derivedFrom":subQ5}),-1.0]])]});}
            var Q153;
            {var subQ0=sQuery(id+"F0.wireOp",EDGE,"E9");var subQ5=sQuery(id+"F0.wireOp",EDGE,"E47");var subQ6=makeQuery(id+"F0.imprint","INTERSECT",VERTEX,{"derivedFrom":[subQ0,subQ5]});Q153=makeQuery(id+"F0.imprint","IMPRINT",FACE,{"disambiguationData":[TD([[makeQuery(id+"F0.imprint","IMPRINT",EDGE,{"disambiguationData":[TD([[subQ6,-1.0]])],"derivedFrom":subQ5}),1.0]])]});}
            var Q154;
            {var subQ0=sQuery(id+"F0.wireOp",EDGE,"E54");var subQ1=sQuery(id+"F0.wireOp",EDGE,"E15");var subQ2=makeQuery(id+"F0.imprint","INTERSECT",VERTEX,{"derivedFrom":[subQ1,subQ0]});Q154=makeQuery(id+"F0.imprint","IMPRINT",FACE,{"disambiguationData":[TD([[makeQuery(id+"F0.imprint","IMPRINT",EDGE,{"disambiguationData":[TD([[subQ2,-1.0]])],"derivedFrom":subQ1}),-1.0]])]});}
            var Q155;
            {var subQ0=sQuery(id+"F0.wireOp",EDGE,"E51");var subQ1=sQuery(id+"F0.wireOp",EDGE,"E4");var subQ2=makeQuery(id+"F0.imprint","INTERSECT",VERTEX,{"derivedFrom":[subQ1,subQ0]});Q155=makeQuery(id+"F0.imprint","IMPRINT",FACE,{"disambiguationData":[TD([[makeQuery(id+"F0.imprint","IMPRINT",EDGE,{"disambiguationData":[TD([[subQ2,-1.0]])],"derivedFrom":subQ1}),-1.0]])]});}
            var Q156;
            {var subQ0=sQuery(id+"F0.wireOp",EDGE,"E61");var subQ1=sQuery(id+"F0.wireOp",EDGE,"E9");var subQ2=makeQuery(id+"F0.imprint","INTERSECT",VERTEX,{"derivedFrom":[subQ1,subQ0]});Q156=makeQuery(id+"F0.imprint","IMPRINT",FACE,{"disambiguationData":[TD([[makeQuery(id+"F0.imprint","IMPRINT",EDGE,{"disambiguationData":[TD([[subQ2,-1.0]])],"derivedFrom":subQ1}),1.0]])]});}
            var Q157;
            {var subQ0=sQuery(id+"F0.wireOp",EDGE,"E53");var subQ1=sQuery(id+"F0.wireOp",EDGE,"E21");var subQ2=makeQuery(id+"F0.imprint","INTERSECT",VERTEX,{"derivedFrom":[subQ1,subQ0]});Q157=makeQuery(id+"F0.imprint","IMPRINT",FACE,{"disambiguationData":[TD([[makeQuery(id+"F0.imprint","IMPRINT",EDGE,{"disambiguationData":[TD([[subQ2,-1.0]])],"derivedFrom":subQ1}),1.0]])]});}
            var Q158;
            {var subQ0=sQuery(id+"F0.wireOp",EDGE,"E50");var subQ1=sQuery(id+"F0.wireOp",EDGE,"E3");var subQ2=makeQuery(id+"F0.imprint","INTERSECT",VERTEX,{"derivedFrom":[subQ1,subQ0]});Q158=makeQuery(id+"F0.imprint","IMPRINT",FACE,{"disambiguationData":[TD([[makeQuery(id+"F0.imprint","IMPRINT",EDGE,{"disambiguationData":[TD([[subQ2,-1.0]])],"derivedFrom":subQ1}),1.0]])]});}
            var Q159;
            {var subQ0=sQuery(id+"F0.wireOp",EDGE,"E52");var subQ1=sQuery(id+"F0.wireOp",EDGE,"E21");var subQ2=makeQuery(id+"F0.imprint","INTERSECT",VERTEX,{"derivedFrom":[subQ1,subQ0]});Q159=makeQuery(id+"F0.imprint","IMPRINT",FACE,{"disambiguationData":[TD([[makeQuery(id+"F0.imprint","IMPRINT",EDGE,{"disambiguationData":[TD([[subQ2,-1.0]])],"derivedFrom":subQ1}),1.0]])]});}
            var Q160;
            {var subQ0=sQuery(id+"F0.wireOp",EDGE,"E53");var subQ1=sQuery(id+"F0.wireOp",EDGE,"E3");var subQ2=makeQuery(id+"F0.imprint","INTERSECT",VERTEX,{"derivedFrom":[subQ1,subQ0]});Q160=makeQuery(id+"F0.imprint","IMPRINT",FACE,{"disambiguationData":[TD([[makeQuery(id+"F0.imprint","IMPRINT",EDGE,{"disambiguationData":[TD([[subQ2,-1.0]])],"derivedFrom":subQ1}),-1.0]])]});}
            var Q161;
            {var subQ0=sQuery(id+"F0.wireOp",EDGE,"E63");var subQ1=sQuery(id+"F0.wireOp",EDGE,"E7");var subQ2=makeQuery(id+"F0.imprint","INTERSECT",VERTEX,{"derivedFrom":[subQ1,subQ0]});Q161=makeQuery(id+"F0.imprint","IMPRINT",FACE,{"disambiguationData":[TD([[makeQuery(id+"F0.imprint","IMPRINT",EDGE,{"disambiguationData":[TD([[subQ2,-1.0]])],"derivedFrom":subQ1}),-1.0]])]});}
            var Q162;
            {var subQ0=sQuery(id+"F0.wireOp",EDGE,"E51");var subQ1=sQuery(id+"F0.wireOp",EDGE,"E15");var subQ2=makeQuery(id+"F0.imprint","INTERSECT",VERTEX,{"derivedFrom":[subQ1,subQ0]});Q162=makeQuery(id+"F0.imprint","IMPRINT",FACE,{"disambiguationData":[TD([[makeQuery(id+"F0.imprint","IMPRINT",EDGE,{"disambiguationData":[TD([[subQ2,-1.0]])],"derivedFrom":subQ1}),-1.0]])]});}
            var Q163;
            {var subQ0=sQuery(id+"F0.wireOp",EDGE,"E23");var subQ1=sQuery(id+"F0.wireOp",EDGE,"E2");var subQ2=makeQuery(id+"F0.imprint","INTERSECT",VERTEX,{"derivedFrom":[subQ1,subQ0]});Q163=makeQuery(id+"F0.imprint","IMPRINT",FACE,{"disambiguationData":[TD([[makeQuery(id+"F0.imprint","IMPRINT",EDGE,{"disambiguationData":[TD([[subQ2,-1.0]])],"derivedFrom":subQ1}),-1.0]])]});}
            var Q164;
            {var subQ0=sQuery(id+"F0.wireOp",EDGE,"E64");var subQ1=sQuery(id+"F0.wireOp",EDGE,"E7");var subQ2=makeQuery(id+"F0.imprint","INTERSECT",VERTEX,{"derivedFrom":[subQ1,subQ0]});Q164=makeQuery(id+"F0.imprint","IMPRINT",FACE,{"disambiguationData":[TD([[makeQuery(id+"F0.imprint","IMPRINT",EDGE,{"disambiguationData":[TD([[subQ2,-1.0]])],"derivedFrom":subQ1}),-1.0]])]});}
            var Q165;
            {var subQ0=sQuery(id+"F0.wireOp",EDGE,"E21");var subQ1=sQuery(id+"F0.wireOp",EDGE,"E1");var subQ2=makeQuery(id+"F0.imprint","INTERSECT",VERTEX,{"derivedFrom":[subQ1,subQ0]});Q165=makeQuery(id+"F0.imprint","IMPRINT",FACE,{"disambiguationData":[TD([[makeQuery(id+"F0.imprint","IMPRINT",EDGE,{"disambiguationData":[TD([[subQ2,-1.0]])],"derivedFrom":subQ1}),1.0]])]});}
            var Q166;
            {var subQ0=sQuery(id+"F0.wireOp",EDGE,"E49");var subQ1=sQuery(id+"F0.wireOp",EDGE,"E5");var subQ2=makeQuery(id+"F0.imprint","INTERSECT",VERTEX,{"derivedFrom":[subQ1,subQ0]});Q166=makeQuery(id+"F0.imprint","IMPRINT",FACE,{"disambiguationData":[TD([[makeQuery(id+"F0.imprint","IMPRINT",EDGE,{"disambiguationData":[TD([[subQ2,-1.0]])],"derivedFrom":subQ1}),-1.0]])]});}
            var Q167;
            {var subQ3=sQuery(id+"F0.wireOp",EDGE,"E1");var subQ7=sQuery(id+"F0.wireOp",EDGE,"E24");var subQ8=makeQuery(id+"F0.imprint","INTERSECT",VERTEX,{"derivedFrom":[subQ3,subQ7]});Q167=makeQuery(id+"F0.imprint","IMPRINT",FACE,{"disambiguationData":[TD([[makeQuery(id+"F0.imprint","IMPRINT",EDGE,{"disambiguationData":[TD([[subQ8,-1.0]])],"derivedFrom":subQ3}),-1.0]])]});}
            var Q168;
            {var subQ0=sQuery(id+"F0.wireOp",EDGE,"E60");var subQ1=sQuery(id+"F0.wireOp",EDGE,"E23");var subQ2=makeQuery(id+"F0.imprint","INTERSECT",VERTEX,{"derivedFrom":[subQ1,subQ0]});Q168=makeQuery(id+"F0.imprint","IMPRINT",FACE,{"disambiguationData":[TD([[makeQuery(id+"F0.imprint","IMPRINT",EDGE,{"disambiguationData":[TD([[subQ2,-1.0]])],"derivedFrom":subQ1}),-1.0]])]});}
            var Q169;
            {var subQ0=sQuery(id+"F0.wireOp",EDGE,"E62");var subQ1=sQuery(id+"F0.wireOp",EDGE,"E2");var subQ2=makeQuery(id+"F0.imprint","INTERSECT",VERTEX,{"derivedFrom":[subQ1,subQ0]});Q169=makeQuery(id+"F0.imprint","IMPRINT",FACE,{"disambiguationData":[TD([[makeQuery(id+"F0.imprint","IMPRINT",EDGE,{"disambiguationData":[TD([[subQ2,-1.0]])],"derivedFrom":subQ1}),1.0]])]});}
            var Q170;
            {var subQ0=sQuery(id+"F0.wireOp",EDGE,"E63");var subQ1=sQuery(id+"F0.wireOp",EDGE,"E13");var subQ2=makeQuery(id+"F0.imprint","INTERSECT",VERTEX,{"derivedFrom":[subQ1,subQ0]});Q170=makeQuery(id+"F0.imprint","IMPRINT",FACE,{"disambiguationData":[TD([[makeQuery(id+"F0.imprint","IMPRINT",EDGE,{"disambiguationData":[TD([[subQ2,-1.0]])],"derivedFrom":subQ1}),1.0]])]});}
            var Q171;
            {var subQ0=sQuery(id+"F0.wireOp",EDGE,"E62");var subQ1=sQuery(id+"F0.wireOp",EDGE,"E3");var subQ2=makeQuery(id+"F0.imprint","INTERSECT",VERTEX,{"derivedFrom":[subQ1,subQ0]});Q171=makeQuery(id+"F0.imprint","IMPRINT",FACE,{"disambiguationData":[TD([[makeQuery(id+"F0.imprint","IMPRINT",EDGE,{"disambiguationData":[TD([[subQ2,-1.0]])],"derivedFrom":subQ1}),-1.0]])]});}
            var Q172;
            {var subQ1=sQuery(id+"F0.wireOp",EDGE,"E0.right");var subQ3=sQuery(id+"F0.wireOp",EDGE,"E24");var subQ4=makeQuery(id+"F0.imprint","INTERSECT",VERTEX,{"derivedFrom":[subQ1,subQ3]});Q172=makeQuery(id+"F0.imprint","IMPRINT",FACE,{"disambiguationData":[TD([[makeQuery(id+"F0.imprint","IMPRINT",EDGE,{"disambiguationData":[TD([[subQ4,-1.0]])],"derivedFrom":subQ3}),-1.0]])]});}
            var Q173;
            {var subQ3=sQuery(id+"F0.wireOp",EDGE,"E60");var subQ6=sQuery(id+"F0.wireOp",EDGE,"E2");var subQ9=makeQuery(id+"F0.imprint","INTERSECT",VERTEX,{"derivedFrom":[subQ6,subQ3]});Q173=makeQuery(id+"F0.imprint","IMPRINT",FACE,{"disambiguationData":[TD([[makeQuery(id+"F0.imprint","IMPRINT",EDGE,{"disambiguationData":[TD([[subQ9,-1.0]])],"derivedFrom":subQ6}),-1.0]])]});}
            var Q174;
            {var subQ0=sQuery(id+"F0.wireOp",EDGE,"E63");var subQ1=sQuery(id+"F0.wireOp",EDGE,"E9");var subQ2=makeQuery(id+"F0.imprint","INTERSECT",VERTEX,{"derivedFrom":[subQ1,subQ0]});Q174=makeQuery(id+"F0.imprint","IMPRINT",FACE,{"disambiguationData":[TD([[makeQuery(id+"F0.imprint","IMPRINT",EDGE,{"disambiguationData":[TD([[subQ2,-1.0]])],"derivedFrom":subQ1}),1.0]])]});}
            var Q175;
            {var subQ1=sQuery(id+"F0.wireOp",EDGE,"E1");var subQ7=sQuery(id+"F0.wireOp",EDGE,"E51");var subQ9=makeQuery(id+"F0.imprint","INTERSECT",VERTEX,{"derivedFrom":[subQ1,subQ7]});Q175=makeQuery(id+"F0.imprint","IMPRINT",FACE,{"disambiguationData":[TD([[makeQuery(id+"F0.imprint","IMPRINT",EDGE,{"disambiguationData":[TD([[subQ9,-1.0]])],"derivedFrom":subQ1}),1.0]])]});}
            var Q176;
            {var subQ0=sQuery(id+"F0.wireOp",EDGE,"E54");var subQ1=sQuery(id+"F0.wireOp",EDGE,"E7");var subQ2=makeQuery(id+"F0.imprint","INTERSECT",VERTEX,{"derivedFrom":[subQ1,subQ0]});Q176=makeQuery(id+"F0.imprint","IMPRINT",FACE,{"disambiguationData":[TD([[makeQuery(id+"F0.imprint","IMPRINT",EDGE,{"disambiguationData":[TD([[subQ2,-1.0]])],"derivedFrom":subQ1}),-1.0]])]});}
            var Q177;
            {var subQ0=sQuery(id+"F0.wireOp",EDGE,"E64");var subQ1=sQuery(id+"F0.wireOp",EDGE,"E5");var subQ2=makeQuery(id+"F0.imprint","INTERSECT",VERTEX,{"derivedFrom":[subQ1,subQ0]});Q177=makeQuery(id+"F0.imprint","IMPRINT",FACE,{"disambiguationData":[TD([[makeQuery(id+"F0.imprint","IMPRINT",EDGE,{"disambiguationData":[TD([[subQ2,-1.0]])],"derivedFrom":subQ1}),-1.0]])]});}
            var Q178;
            {var subQ0=sQuery(id+"F0.wireOp",EDGE,"E14");Q178=makeQuery(id+"F0.imprint","IMPRINT",FACE,{"disambiguationData":[TD([[makeQuery(id+"F0.imprint","IMPRINT",EDGE,{"derivedFrom":subQ0}),1.0]])]});}
            var Q179;
            {var subQ1=sQuery(id+"F0.wireOp",EDGE,"E0.right");var subQ5=sQuery(id+"F0.wireOp",EDGE,"E3");var subQ9=makeQuery(id+"F0.imprint","INTERSECT",VERTEX,{"derivedFrom":[subQ1,subQ5]});Q179=makeQuery(id+"F0.imprint","IMPRINT",FACE,{"disambiguationData":[TD([[makeQuery(id+"F0.imprint","IMPRINT",EDGE,{"disambiguationData":[TD([[subQ9,-1.0]])],"derivedFrom":subQ1}),1.0]])]});}
            var Q180;
            {var subQ0=sQuery(id+"F0.wireOp",EDGE,"E53");var subQ1=sQuery(id+"F0.wireOp",EDGE,"E5");var subQ2=makeQuery(id+"F0.imprint","INTERSECT",VERTEX,{"derivedFrom":[subQ1,subQ0]});Q180=makeQuery(id+"F0.imprint","IMPRINT",FACE,{"disambiguationData":[TD([[makeQuery(id+"F0.imprint","IMPRINT",EDGE,{"disambiguationData":[TD([[subQ2,-1.0]])],"derivedFrom":subQ1}),-1.0]])]});}
            var Q181;
            {var subQ0=sQuery(id+"F0.wireOp",EDGE,"E54");var subQ1=sQuery(id+"F0.wireOp",EDGE,"E17");var subQ2=makeQuery(id+"F0.imprint","INTERSECT",VERTEX,{"derivedFrom":[subQ1,subQ0]});Q181=makeQuery(id+"F0.imprint","IMPRINT",FACE,{"disambiguationData":[TD([[makeQuery(id+"F0.imprint","IMPRINT",EDGE,{"disambiguationData":[TD([[subQ2,-1.0]])],"derivedFrom":subQ1}),1.0]])]});}
            var Q182;
            {var subQ0=sQuery(id+"F0.wireOp",EDGE,"E60");var subQ1=sQuery(id+"F0.wireOp",EDGE,"E4");var subQ2=makeQuery(id+"F0.imprint","INTERSECT",VERTEX,{"derivedFrom":[subQ1,subQ0]});Q182=makeQuery(id+"F0.imprint","IMPRINT",FACE,{"disambiguationData":[TD([[makeQuery(id+"F0.imprint","IMPRINT",EDGE,{"disambiguationData":[TD([[subQ2,-1.0]])],"derivedFrom":subQ1}),-1.0]])]});}
            var Q183;
            {var subQ0=sQuery(id+"F0.wireOp",EDGE,"E49");var subQ1=sQuery(id+"F0.wireOp",EDGE,"E11");var subQ2=makeQuery(id+"F0.imprint","INTERSECT",VERTEX,{"derivedFrom":[subQ1,subQ0]});Q183=makeQuery(id+"F0.imprint","IMPRINT",FACE,{"disambiguationData":[TD([[makeQuery(id+"F0.imprint","IMPRINT",EDGE,{"disambiguationData":[TD([[subQ2,-1.0]])],"derivedFrom":subQ1}),-1.0]])]});}
            var Q184;
            {var subQ0=sQuery(id+"F0.wireOp",EDGE,"E63");var subQ1=sQuery(id+"F0.wireOp",EDGE,"E3");var subQ2=makeQuery(id+"F0.imprint","INTERSECT",VERTEX,{"derivedFrom":[subQ1,subQ0]});Q184=makeQuery(id+"F0.imprint","IMPRINT",FACE,{"disambiguationData":[TD([[makeQuery(id+"F0.imprint","IMPRINT",EDGE,{"disambiguationData":[TD([[subQ2,-1.0]])],"derivedFrom":subQ1}),-1.0]])]});}
            var Q185;
            {var subQ0=sQuery(id+"F0.wireOp",EDGE,"E60");var subQ1=sQuery(id+"F0.wireOp",EDGE,"E3");var subQ2=makeQuery(id+"F0.imprint","INTERSECT",VERTEX,{"derivedFrom":[subQ1,subQ0]});Q185=makeQuery(id+"F0.imprint","IMPRINT",FACE,{"disambiguationData":[TD([[makeQuery(id+"F0.imprint","IMPRINT",EDGE,{"disambiguationData":[TD([[subQ2,-1.0]])],"derivedFrom":subQ1}),1.0]])]});}
            var Q186;
            {var subQ0=sQuery(id+"F0.wireOp",EDGE,"E60");var subQ1=sQuery(id+"F0.wireOp",EDGE,"E3");var subQ2=makeQuery(id+"F0.imprint","INTERSECT",VERTEX,{"derivedFrom":[subQ1,subQ0]});Q186=makeQuery(id+"F0.imprint","IMPRINT",FACE,{"disambiguationData":[TD([[makeQuery(id+"F0.imprint","IMPRINT",EDGE,{"disambiguationData":[TD([[subQ2,-1.0]])],"derivedFrom":subQ1}),-1.0]])]});}
            var Q187;
            {var subQ5=sQuery(id+"F0.wireOp",EDGE,"E63");var subQ7=sQuery(id+"F0.wireOp",EDGE,"E2");var subQ9=makeQuery(id+"F0.imprint","INTERSECT",VERTEX,{"derivedFrom":[subQ7,subQ5]});Q187=makeQuery(id+"F0.imprint","IMPRINT",FACE,{"disambiguationData":[TD([[makeQuery(id+"F0.imprint","IMPRINT",EDGE,{"disambiguationData":[TD([[subQ9,-1.0]])],"derivedFrom":subQ7}),-1.0]])]});}
            var Q188;
            {var subQ0=sQuery(id+"F0.wireOp",EDGE,"E60");var subQ1=sQuery(id+"F0.wireOp",EDGE,"E11");var subQ2=makeQuery(id+"F0.imprint","INTERSECT",VERTEX,{"derivedFrom":[subQ1,subQ0]});Q188=makeQuery(id+"F0.imprint","IMPRINT",FACE,{"disambiguationData":[TD([[makeQuery(id+"F0.imprint","IMPRINT",EDGE,{"disambiguationData":[TD([[subQ2,-1.0]])],"derivedFrom":subQ1}),-1.0]])]});}
            var Q189;
            {var subQ0=sQuery(id+"F0.wireOp",EDGE,"E55");var subQ1=sQuery(id+"F0.wireOp",EDGE,"E23");var subQ2=makeQuery(id+"F0.imprint","INTERSECT",VERTEX,{"derivedFrom":[subQ1,subQ0]});Q189=makeQuery(id+"F0.imprint","IMPRINT",FACE,{"disambiguationData":[TD([[makeQuery(id+"F0.imprint","IMPRINT",EDGE,{"disambiguationData":[TD([[subQ2,-1.0]])],"derivedFrom":subQ1}),-1.0]])]});}
            var Q190;
            {var subQ1=sQuery(id+"F0.wireOp",EDGE,"E0.left");var subQ3=sQuery(id+"F0.wireOp",EDGE,"E23");var subQ4=makeQuery(id+"F0.imprint","INTERSECT",VERTEX,{"derivedFrom":[subQ1,subQ3]});Q190=makeQuery(id+"F0.imprint","IMPRINT",FACE,{"disambiguationData":[TD([[makeQuery(id+"F0.imprint","IMPRINT",EDGE,{"disambiguationData":[TD([[subQ4,1.0]])],"derivedFrom":subQ3}),1.0]])]});}
            var Q191;
            {var subQ1=sQuery(id+"F0.wireOp",EDGE,"E0.top");var subQ6=sQuery(id+"F0.wireOp",EDGE,"E30");var subQ9=makeQuery(id+"F0.imprint","INTERSECT",VERTEX,{"disambiguationData":[OD(0.0)],"derivedFrom":[subQ1,subQ6]});Q191=makeQuery(id+"F0.imprint","IMPRINT",FACE,{"disambiguationData":[TD([[makeQuery(id+"F0.imprint","IMPRINT",EDGE,{"disambiguationData":[TD([[subQ9,1.0]])],"derivedFrom":subQ1}),-1.0]])]});}
            var Q192;
            {var subQ1=sQuery(id+"F0.wireOp",EDGE,"E2");var subQ5=sQuery(id+"F0.wireOp",EDGE,"E5");var subQ6=makeQuery(id+"F0.imprint","INTERSECT",VERTEX,{"derivedFrom":[subQ1,subQ5]});Q192=makeQuery(id+"F0.imprint","IMPRINT",FACE,{"disambiguationData":[TD([[makeQuery(id+"F0.imprint","IMPRINT",EDGE,{"disambiguationData":[TD([[subQ6,-1.0]])],"derivedFrom":subQ1}),1.0]])]});}
            var Q193;
            {var subQ5=sQuery(id+"F0.wireOp",EDGE,"E1");var subQ7=sQuery(id+"F0.wireOp",EDGE,"E6");var subQ8=makeQuery(id+"F0.imprint","INTERSECT",VERTEX,{"derivedFrom":[subQ5,subQ7]});Q193=makeQuery(id+"F0.imprint","IMPRINT",FACE,{"disambiguationData":[TD([[makeQuery(id+"F0.imprint","IMPRINT",EDGE,{"disambiguationData":[TD([[subQ8,-1.0]])],"derivedFrom":subQ5}),-1.0]])]});}
            var Q194;
            {var subQ0=sQuery(id+"F0.wireOp",EDGE,"E55");var subQ1=sQuery(id+"F0.wireOp",EDGE,"E19");var subQ2=makeQuery(id+"F0.imprint","INTERSECT",VERTEX,{"derivedFrom":[subQ1,subQ0]});Q194=makeQuery(id+"F0.imprint","IMPRINT",FACE,{"disambiguationData":[TD([[makeQuery(id+"F0.imprint","IMPRINT",EDGE,{"disambiguationData":[TD([[subQ2,-1.0]])],"derivedFrom":subQ1}),-1.0]])]});}
            var Q195;
            {var subQ0=sQuery(id+"F0.wireOp",EDGE,"E4");var subQ1=sQuery(id+"F0.wireOp",EDGE,"E0.right");var subQ2=makeQuery(id+"F0.imprint","INTERSECT",VERTEX,{"derivedFrom":[subQ1,subQ0]});Q195=makeQuery(id+"F0.imprint","IMPRINT",FACE,{"disambiguationData":[TD([[makeQuery(id+"F0.imprint","IMPRINT",EDGE,{"disambiguationData":[TD([[subQ2,-1.0]])],"derivedFrom":subQ1}),1.0]])]});}
            var Q196;
            {var subQ5=sQuery(id+"F0.wireOp",EDGE,"E51");var subQ7=sQuery(id+"F0.wireOp",EDGE,"E2");var subQ9=makeQuery(id+"F0.imprint","INTERSECT",VERTEX,{"derivedFrom":[subQ7,subQ5]});Q196=makeQuery(id+"F0.imprint","IMPRINT",FACE,{"disambiguationData":[TD([[makeQuery(id+"F0.imprint","IMPRINT",EDGE,{"disambiguationData":[TD([[subQ9,-1.0]])],"derivedFrom":subQ7}),-1.0]])]});}
            var Q197;
            {var subQ0=sQuery(id+"F0.wireOp",EDGE,"E49");var subQ1=sQuery(id+"F0.wireOp",EDGE,"E9");var subQ2=makeQuery(id+"F0.imprint","INTERSECT",VERTEX,{"derivedFrom":[subQ1,subQ0]});Q197=makeQuery(id+"F0.imprint","IMPRINT",FACE,{"disambiguationData":[TD([[makeQuery(id+"F0.imprint","IMPRINT",EDGE,{"disambiguationData":[TD([[subQ2,-1.0]])],"derivedFrom":subQ1}),1.0]])]});}
            var Q198;
            {var subQ0=sQuery(id+"F0.wireOp",EDGE,"E22");Q198=makeQuery(id+"F0.imprint","IMPRINT",FACE,{"disambiguationData":[TD([[makeQuery(id+"F0.imprint","IMPRINT",EDGE,{"derivedFrom":subQ0}),1.0]])]});}
            var Q199;
            {var subQ1=sQuery(id+"F0.wireOp",EDGE,"E0.left");var subQ3=sQuery(id+"F0.wireOp",EDGE,"E24");var subQ4=makeQuery(id+"F0.imprint","INTERSECT",VERTEX,{"derivedFrom":[subQ1,subQ3]});Q199=makeQuery(id+"F0.imprint","IMPRINT",FACE,{"disambiguationData":[TD([[makeQuery(id+"F0.imprint","IMPRINT",EDGE,{"disambiguationData":[TD([[subQ4,1.0]])],"derivedFrom":subQ3}),-1.0]])]});}
            var Q200;
            {var subQ7=sQuery(id+"F0.wireOp",EDGE,"E59");Q200=makeQuery(id+"F0.imprint","IMPRINT",FACE,{"disambiguationData":[TD([[makeQuery(id+"F0.imprint","IMPRINT",EDGE,{"derivedFrom":subQ7}),-1.0]])]});}
            var Q201;
            {var subQ0=sQuery(id+"F0.wireOp",EDGE,"E50");var subQ1=sQuery(id+"F0.wireOp",EDGE,"E11");var subQ2=makeQuery(id+"F0.imprint","INTERSECT",VERTEX,{"derivedFrom":[subQ1,subQ0]});Q201=makeQuery(id+"F0.imprint","IMPRINT",FACE,{"disambiguationData":[TD([[makeQuery(id+"F0.imprint","IMPRINT",EDGE,{"disambiguationData":[TD([[subQ2,-1.0]])],"derivedFrom":subQ1}),-1.0]])]});}
            var Q202;
            {var subQ0=sQuery(id+"F0.wireOp",EDGE,"E6");var subQ1=sQuery(id+"F0.wireOp",EDGE,"E0.left");var subQ2=makeQuery(id+"F0.imprint","INTERSECT",VERTEX,{"derivedFrom":[subQ1,subQ0]});Q202=makeQuery(id+"F0.imprint","IMPRINT",FACE,{"disambiguationData":[TD([[makeQuery(id+"F0.imprint","IMPRINT",EDGE,{"disambiguationData":[TD([[subQ2,1.0]])],"derivedFrom":subQ0}),-1.0]])]});}
            var Q203;
            {var subQ0=sQuery(id+"F0.wireOp",EDGE,"E60");var subQ1=sQuery(id+"F0.wireOp",EDGE,"E19");var subQ2=makeQuery(id+"F0.imprint","INTERSECT",VERTEX,{"derivedFrom":[subQ1,subQ0]});Q203=makeQuery(id+"F0.imprint","IMPRINT",FACE,{"disambiguationData":[TD([[makeQuery(id+"F0.imprint","IMPRINT",EDGE,{"disambiguationData":[TD([[subQ2,-1.0]])],"derivedFrom":subQ1}),-1.0]])]});}
            var Q204;
            {var subQ0=sQuery(id+"F0.wireOp",EDGE,"E63");var subQ1=sQuery(id+"F0.wireOp",EDGE,"E11");var subQ2=makeQuery(id+"F0.imprint","INTERSECT",VERTEX,{"derivedFrom":[subQ1,subQ0]});Q204=makeQuery(id+"F0.imprint","IMPRINT",FACE,{"disambiguationData":[TD([[makeQuery(id+"F0.imprint","IMPRINT",EDGE,{"disambiguationData":[TD([[subQ2,-1.0]])],"derivedFrom":subQ1}),-1.0]])]});}
            var Q205;
            {var subQ5=sQuery(id+"F0.wireOp",EDGE,"E64");var subQ7=sQuery(id+"F0.wireOp",EDGE,"E2");var subQ9=makeQuery(id+"F0.imprint","INTERSECT",VERTEX,{"derivedFrom":[subQ7,subQ5]});Q205=makeQuery(id+"F0.imprint","IMPRINT",FACE,{"disambiguationData":[TD([[makeQuery(id+"F0.imprint","IMPRINT",EDGE,{"disambiguationData":[TD([[subQ9,-1.0]])],"derivedFrom":subQ7}),-1.0]])]});}
            var Q206;
            {var subQ0=sQuery(id+"F0.wireOp",EDGE,"E49");var subQ1=sQuery(id+"F0.wireOp",EDGE,"E7");var subQ2=makeQuery(id+"F0.imprint","INTERSECT",VERTEX,{"derivedFrom":[subQ1,subQ0]});Q206=makeQuery(id+"F0.imprint","IMPRINT",FACE,{"disambiguationData":[TD([[makeQuery(id+"F0.imprint","IMPRINT",EDGE,{"disambiguationData":[TD([[subQ2,-1.0]])],"derivedFrom":subQ1}),-1.0]])]});}
            var Q207;
            {var subQ0=sQuery(id+"F0.wireOp",EDGE,"E51");var subQ1=sQuery(id+"F0.wireOp",EDGE,"E21");var subQ2=makeQuery(id+"F0.imprint","INTERSECT",VERTEX,{"derivedFrom":[subQ1,subQ0]});Q207=makeQuery(id+"F0.imprint","IMPRINT",FACE,{"disambiguationData":[TD([[makeQuery(id+"F0.imprint","IMPRINT",EDGE,{"disambiguationData":[TD([[subQ2,-1.0]])],"derivedFrom":subQ1}),1.0]])]});}
            var Q208;
            {var subQ3=sQuery(id+"F0.wireOp",EDGE,"E3");var subQ7=sQuery(id+"F0.wireOp",EDGE,"E64");var subQ9=makeQuery(id+"F0.imprint","INTERSECT",VERTEX,{"derivedFrom":[subQ3,subQ7]});Q208=makeQuery(id+"F0.imprint","IMPRINT",FACE,{"disambiguationData":[TD([[makeQuery(id+"F0.imprint","IMPRINT",EDGE,{"disambiguationData":[TD([[subQ9,-1.0]])],"derivedFrom":subQ3}),1.0]])]});}
            var Q209;
            {var subQ5=sQuery(id+"F0.wireOp",EDGE,"E17");var subQ6=sQuery(id+"F0.wireOp",EDGE,"E1");var subQ7=makeQuery(id+"F0.imprint","INTERSECT",VERTEX,{"derivedFrom":[subQ6,subQ5]});Q209=makeQuery(id+"F0.imprint","IMPRINT",FACE,{"disambiguationData":[TD([[makeQuery(id+"F0.imprint","IMPRINT",EDGE,{"disambiguationData":[TD([[subQ7,-1.0]])],"derivedFrom":subQ6}),-1.0]])]});}
            var Q210;
            {var subQ1=sQuery(id+"F0.wireOp",EDGE,"E1");var subQ7=sQuery(id+"F0.wireOp",EDGE,"E4");var subQ8=makeQuery(id+"F0.imprint","INTERSECT",VERTEX,{"derivedFrom":[subQ1,subQ7]});Q210=makeQuery(id+"F0.imprint","IMPRINT",FACE,{"disambiguationData":[TD([[makeQuery(id+"F0.imprint","IMPRINT",EDGE,{"disambiguationData":[TD([[subQ8,-1.0]])],"derivedFrom":subQ1}),-1.0]])]});}
            var Q211;
            {var subQ0=sQuery(id+"F0.wireOp",EDGE,"E64");var subQ1=sQuery(id+"F0.wireOp",EDGE,"E15");var subQ2=makeQuery(id+"F0.imprint","INTERSECT",VERTEX,{"derivedFrom":[subQ1,subQ0]});Q211=makeQuery(id+"F0.imprint","IMPRINT",FACE,{"disambiguationData":[TD([[makeQuery(id+"F0.imprint","IMPRINT",EDGE,{"disambiguationData":[TD([[subQ2,-1.0]])],"derivedFrom":subQ1}),-1.0]])]});}
            var Q212;
            {var subQ0=sQuery(id+"F0.wireOp",EDGE,"E9");var subQ1=sQuery(id+"F0.wireOp",EDGE,"E2");var subQ2=makeQuery(id+"F0.imprint","INTERSECT",VERTEX,{"derivedFrom":[subQ1,subQ0]});Q212=makeQuery(id+"F0.imprint","IMPRINT",FACE,{"disambiguationData":[TD([[makeQuery(id+"F0.imprint","IMPRINT",EDGE,{"disambiguationData":[TD([[subQ2,-1.0]])],"derivedFrom":subQ1}),-1.0]])]});}
            var Q213;
            {var subQ0=sQuery(id+"F0.wireOp",EDGE,"E55");var subQ1=sQuery(id+"F0.wireOp",EDGE,"E17");var subQ2=makeQuery(id+"F0.imprint","INTERSECT",VERTEX,{"derivedFrom":[subQ1,subQ0]});Q213=makeQuery(id+"F0.imprint","IMPRINT",FACE,{"disambiguationData":[TD([[makeQuery(id+"F0.imprint","IMPRINT",EDGE,{"disambiguationData":[TD([[subQ2,-1.0]])],"derivedFrom":subQ1}),1.0]])]});}
            var Q214;
            {var subQ0=sQuery(id+"F0.wireOp",EDGE,"E5");var subQ1=sQuery(id+"F0.wireOp",EDGE,"E0.left");var subQ2=makeQuery(id+"F0.imprint","INTERSECT",VERTEX,{"derivedFrom":[subQ1,subQ0]});Q214=makeQuery(id+"F0.imprint","IMPRINT",FACE,{"disambiguationData":[TD([[makeQuery(id+"F0.imprint","IMPRINT",EDGE,{"disambiguationData":[TD([[subQ2,-1.0]])],"derivedFrom":subQ1}),-1.0]])]});}
            var Q215;
            {var subQ1=sQuery(id+"F0.wireOp",EDGE,"E0.right");var subQ3=sQuery(id+"F0.wireOp",EDGE,"E3");var subQ4=makeQuery(id+"F0.imprint","INTERSECT",VERTEX,{"derivedFrom":[subQ1,subQ3]});Q215=makeQuery(id+"F0.imprint","IMPRINT",FACE,{"disambiguationData":[TD([[makeQuery(id+"F0.imprint","IMPRINT",EDGE,{"disambiguationData":[TD([[subQ4,-1.0]])],"derivedFrom":subQ3}),1.0]])]});}
            var Q216;
            {var subQ5=sQuery(id+"F0.wireOp",EDGE,"E53");var subQ6=sQuery(id+"F0.wireOp",EDGE,"E2");var subQ7=makeQuery(id+"F0.imprint","INTERSECT",VERTEX,{"derivedFrom":[subQ6,subQ5]});Q216=makeQuery(id+"F0.imprint","IMPRINT",FACE,{"disambiguationData":[TD([[makeQuery(id+"F0.imprint","IMPRINT",EDGE,{"disambiguationData":[TD([[subQ7,-1.0]])],"derivedFrom":subQ6}),-1.0]])]});}
            var Q217;
            {var subQ0=sQuery(id+"F0.wireOp",EDGE,"E55");var subQ1=sQuery(id+"F0.wireOp",EDGE,"E15");var subQ2=makeQuery(id+"F0.imprint","INTERSECT",VERTEX,{"derivedFrom":[subQ1,subQ0]});Q217=makeQuery(id+"F0.imprint","IMPRINT",FACE,{"disambiguationData":[TD([[makeQuery(id+"F0.imprint","IMPRINT",EDGE,{"disambiguationData":[TD([[subQ2,-1.0]])],"derivedFrom":subQ1}),-1.0]])]});}
            var Q218;
            {var subQ5=sQuery(id+"F0.wireOp",EDGE,"E1");var subQ7=sQuery(id+"F0.wireOp",EDGE,"E62");var subQ9=makeQuery(id+"F0.imprint","INTERSECT",VERTEX,{"derivedFrom":[subQ5,subQ7]});Q218=makeQuery(id+"F0.imprint","IMPRINT",FACE,{"disambiguationData":[TD([[makeQuery(id+"F0.imprint","IMPRINT",EDGE,{"disambiguationData":[TD([[subQ9,-1.0]])],"derivedFrom":subQ5}),1.0]])]});}
            var Q219;
            {var subQ0=sQuery(id+"F0.wireOp",EDGE,"E61");var subQ1=sQuery(id+"F0.wireOp",EDGE,"E19");var subQ2=makeQuery(id+"F0.imprint","INTERSECT",VERTEX,{"derivedFrom":[subQ1,subQ0]});Q219=makeQuery(id+"F0.imprint","IMPRINT",FACE,{"disambiguationData":[TD([[makeQuery(id+"F0.imprint","IMPRINT",EDGE,{"disambiguationData":[TD([[subQ2,-1.0]])],"derivedFrom":subQ1}),-1.0]])]});}
            var Q220;
            {var subQ0=sQuery(id+"F0.wireOp",EDGE,"E15");var subQ1=sQuery(id+"F0.wireOp",EDGE,"E1");var subQ2=makeQuery(id+"F0.imprint","INTERSECT",VERTEX,{"derivedFrom":[subQ1,subQ0]});Q220=makeQuery(id+"F0.imprint","IMPRINT",FACE,{"disambiguationData":[TD([[makeQuery(id+"F0.imprint","IMPRINT",EDGE,{"disambiguationData":[TD([[subQ2,-1.0]])],"derivedFrom":subQ1}),1.0]])]});}
            var Q221;
            {var subQ5=sQuery(id+"F0.wireOp",EDGE,"E1");var subQ7=sQuery(id+"F0.wireOp",EDGE,"E49");var subQ9=makeQuery(id+"F0.imprint","INTERSECT",VERTEX,{"derivedFrom":[subQ5,subQ7]});Q221=makeQuery(id+"F0.imprint","IMPRINT",FACE,{"disambiguationData":[TD([[makeQuery(id+"F0.imprint","IMPRINT",EDGE,{"disambiguationData":[TD([[subQ9,-1.0]])],"derivedFrom":subQ5}),1.0]])]});}
            var Q222;
            {var subQ0=sQuery(id+"F0.wireOp",EDGE,"E55");var subQ1=sQuery(id+"F0.wireOp",EDGE,"E3");var subQ2=makeQuery(id+"F0.imprint","INTERSECT",VERTEX,{"derivedFrom":[subQ1,subQ0]});Q222=makeQuery(id+"F0.imprint","IMPRINT",FACE,{"disambiguationData":[TD([[makeQuery(id+"F0.imprint","IMPRINT",EDGE,{"disambiguationData":[TD([[subQ2,-1.0]])],"derivedFrom":subQ1}),1.0]])]});}
            var Q223;
            {var subQ0=sQuery(id+"F0.wireOp",EDGE,"E51");var subQ1=sQuery(id+"F0.wireOp",EDGE,"E7");var subQ2=makeQuery(id+"F0.imprint","INTERSECT",VERTEX,{"derivedFrom":[subQ1,subQ0]});Q223=makeQuery(id+"F0.imprint","IMPRINT",FACE,{"disambiguationData":[TD([[makeQuery(id+"F0.imprint","IMPRINT",EDGE,{"disambiguationData":[TD([[subQ2,-1.0]])],"derivedFrom":subQ1}),-1.0]])]});}
            var Q224;
            {var subQ0=sQuery(id+"F0.wireOp",EDGE,"E3");var subQ1=sQuery(id+"F0.wireOp",EDGE,"E1");var subQ2=makeQuery(id+"F0.imprint","INTERSECT",VERTEX,{"derivedFrom":[subQ1,subQ0]});Q224=makeQuery(id+"F0.imprint","IMPRINT",FACE,{"disambiguationData":[TD([[makeQuery(id+"F0.imprint","IMPRINT",EDGE,{"disambiguationData":[TD([[subQ2,-1.0]])],"derivedFrom":subQ0}),1.0]])]});}
            var Q225;
            {var subQ0=sQuery(id+"F0.wireOp",EDGE,"E64");var subQ1=sQuery(id+"F0.wireOp",EDGE,"E11");var subQ2=makeQuery(id+"F0.imprint","INTERSECT",VERTEX,{"derivedFrom":[subQ1,subQ0]});Q225=makeQuery(id+"F0.imprint","IMPRINT",FACE,{"disambiguationData":[TD([[makeQuery(id+"F0.imprint","IMPRINT",EDGE,{"disambiguationData":[TD([[subQ2,-1.0]])],"derivedFrom":subQ1}),-1.0]])]});}
            var Q226;
            {var subQ0=sQuery(id+"F0.wireOp",EDGE,"E17");var subQ5=sQuery(id+"F0.wireOp",EDGE,"E47");var subQ6=makeQuery(id+"F0.imprint","INTERSECT",VERTEX,{"derivedFrom":[subQ0,subQ5]});Q226=makeQuery(id+"F0.imprint","IMPRINT",FACE,{"disambiguationData":[TD([[makeQuery(id+"F0.imprint","IMPRINT",EDGE,{"disambiguationData":[TD([[subQ6,-1.0]])],"derivedFrom":subQ5}),1.0]])]});}
            var Q227;
            {var subQ1=sQuery(id+"F0.wireOp",EDGE,"E1");var subQ5=sQuery(id+"F0.wireOp",EDGE,"E15");var subQ6=makeQuery(id+"F0.imprint","INTERSECT",VERTEX,{"derivedFrom":[subQ1,subQ5]});Q227=makeQuery(id+"F0.imprint","IMPRINT",FACE,{"disambiguationData":[TD([[makeQuery(id+"F0.imprint","IMPRINT",EDGE,{"disambiguationData":[TD([[subQ6,-1.0]])],"derivedFrom":subQ1}),-1.0]])]});}
            var Q228;
            {var subQ0=sQuery(id+"F0.wireOp",EDGE,"E48");var subQ1=sQuery(id+"F0.wireOp",EDGE,"E11");var subQ2=makeQuery(id+"F0.imprint","INTERSECT",VERTEX,{"derivedFrom":[subQ1,subQ0]});Q228=makeQuery(id+"F0.imprint","IMPRINT",FACE,{"disambiguationData":[TD([[makeQuery(id+"F0.imprint","IMPRINT",EDGE,{"disambiguationData":[TD([[subQ2,-1.0]])],"derivedFrom":subQ1}),-1.0]])]});}
            var Q229;
            {var subQ0=sQuery(id+"F0.wireOp",EDGE,"E63");var subQ1=sQuery(id+"F0.wireOp",EDGE,"E0.top");var subQ2=makeQuery(id+"F0.imprint","INTERSECT",VERTEX,{"derivedFrom":[subQ1,subQ0]});Q229=makeQuery(id+"F0.imprint","IMPRINT",FACE,{"disambiguationData":[TD([[makeQuery(id+"F0.imprint","IMPRINT",EDGE,{"disambiguationData":[TD([[subQ2,-1.0]])],"derivedFrom":subQ1}),-1.0]])]});}
            var Q230;
            {var subQ0=sQuery(id+"F0.wireOp",EDGE,"E50");var subQ1=sQuery(id+"F0.wireOp",EDGE,"E23");var subQ2=makeQuery(id+"F0.imprint","INTERSECT",VERTEX,{"derivedFrom":[subQ1,subQ0]});Q230=makeQuery(id+"F0.imprint","IMPRINT",FACE,{"disambiguationData":[TD([[makeQuery(id+"F0.imprint","IMPRINT",EDGE,{"disambiguationData":[TD([[subQ2,-1.0]])],"derivedFrom":subQ1}),-1.0]])]});}
            var Q231;
            {var subQ0=sQuery(id+"F0.wireOp",EDGE,"E61");var subQ5=sQuery(id+"F0.wireOp",EDGE,"E2");var subQ6=makeQuery(id+"F0.imprint","INTERSECT",VERTEX,{"derivedFrom":[subQ5,subQ0]});Q231=makeQuery(id+"F0.imprint","IMPRINT",FACE,{"disambiguationData":[TD([[makeQuery(id+"F0.imprint","IMPRINT",EDGE,{"disambiguationData":[TD([[subQ6,-1.0]])],"derivedFrom":subQ5}),-1.0]])]});}
            var Q232;
            {var subQ3=sQuery(id+"F0.wireOp",EDGE,"E55");var subQ5=sQuery(id+"F0.wireOp",EDGE,"E24");var subQ6=makeQuery(id+"F0.imprint","INTERSECT",VERTEX,{"derivedFrom":[subQ5,subQ3]});Q232=makeQuery(id+"F0.imprint","IMPRINT",FACE,{"disambiguationData":[TD([[makeQuery(id+"F0.imprint","IMPRINT",EDGE,{"disambiguationData":[TD([[subQ6,-1.0]])],"derivedFrom":subQ5}),-1.0]])]});}
            var Q233;
            {var subQ0=sQuery(id+"F0.wireOp",EDGE,"E6");var subQ1=sQuery(id+"F0.wireOp",EDGE,"E0.right");var subQ2=makeQuery(id+"F0.imprint","INTERSECT",VERTEX,{"derivedFrom":[subQ1,subQ0]});Q233=makeQuery(id+"F0.imprint","IMPRINT",FACE,{"disambiguationData":[TD([[makeQuery(id+"F0.imprint","IMPRINT",EDGE,{"disambiguationData":[TD([[subQ2,-1.0]])],"derivedFrom":subQ1}),1.0]])]});}
            var Q234;
            {var subQ0=sQuery(id+"F0.wireOp",EDGE,"E63");var subQ1=sQuery(id+"F0.wireOp",EDGE,"E6");var subQ2=makeQuery(id+"F0.imprint","INTERSECT",VERTEX,{"derivedFrom":[subQ1,subQ0]});Q234=makeQuery(id+"F0.imprint","IMPRINT",FACE,{"disambiguationData":[TD([[makeQuery(id+"F0.imprint","IMPRINT",EDGE,{"disambiguationData":[TD([[subQ2,-1.0]])],"derivedFrom":subQ1}),-1.0]])]});}
            var Q235;
            {var subQ0=sQuery(id+"F0.wireOp",EDGE,"E51");var subQ1=sQuery(id+"F0.wireOp",EDGE,"E23");var subQ2=makeQuery(id+"F0.imprint","INTERSECT",VERTEX,{"derivedFrom":[subQ1,subQ0]});Q235=makeQuery(id+"F0.imprint","IMPRINT",FACE,{"disambiguationData":[TD([[makeQuery(id+"F0.imprint","IMPRINT",EDGE,{"disambiguationData":[TD([[subQ2,-1.0]])],"derivedFrom":subQ1}),-1.0]])]});}
            var Q236;
            {var subQ0=sQuery(id+"F0.wireOp",EDGE,"E61");var subQ1=sQuery(id+"F0.wireOp",EDGE,"E3");var subQ2=makeQuery(id+"F0.imprint","INTERSECT",VERTEX,{"derivedFrom":[subQ1,subQ0]});Q236=makeQuery(id+"F0.imprint","IMPRINT",FACE,{"disambiguationData":[TD([[makeQuery(id+"F0.imprint","IMPRINT",EDGE,{"disambiguationData":[TD([[subQ2,-1.0]])],"derivedFrom":subQ1}),1.0]])]});}
            var Q237;
            {var subQ0=sQuery(id+"F0.wireOp",EDGE,"E61");var subQ1=sQuery(id+"F0.wireOp",EDGE,"E23");var subQ2=makeQuery(id+"F0.imprint","INTERSECT",VERTEX,{"derivedFrom":[subQ1,subQ0]});Q237=makeQuery(id+"F0.imprint","IMPRINT",FACE,{"disambiguationData":[TD([[makeQuery(id+"F0.imprint","IMPRINT",EDGE,{"disambiguationData":[TD([[subQ2,-1.0]])],"derivedFrom":subQ1}),-1.0]])]});}
            var Q238;
            {var subQ0=sQuery(id+"F0.wireOp",EDGE,"E55");var subQ1=sQuery(id+"F0.wireOp",EDGE,"E6");var subQ2=makeQuery(id+"F0.imprint","INTERSECT",VERTEX,{"derivedFrom":[subQ1,subQ0]});Q238=makeQuery(id+"F0.imprint","IMPRINT",FACE,{"disambiguationData":[TD([[makeQuery(id+"F0.imprint","IMPRINT",EDGE,{"disambiguationData":[TD([[subQ2,-1.0]])],"derivedFrom":subQ1}),-1.0]])]});}
            var Q239;
            {var subQ0=sQuery(id+"F0.wireOp",EDGE,"E2");var subQ1=sQuery(id+"F0.wireOp",EDGE,"E1");var subQ2=makeQuery(id+"F0.imprint","INTERSECT",VERTEX,{"derivedFrom":[subQ1,subQ0]});Q239=makeQuery(id+"F0.imprint","IMPRINT",FACE,{"disambiguationData":[TD([[makeQuery(id+"F0.imprint","IMPRINT",EDGE,{"disambiguationData":[TD([[subQ2,-1.0]])],"derivedFrom":subQ1}),1.0]])]});}
            var Q240;
            {var subQ0=sQuery(id+"F0.wireOp",EDGE,"E62");var subQ1=sQuery(id+"F0.wireOp",EDGE,"E2");var subQ2=makeQuery(id+"F0.imprint","INTERSECT",VERTEX,{"derivedFrom":[subQ1,subQ0]});Q240=makeQuery(id+"F0.imprint","IMPRINT",FACE,{"disambiguationData":[TD([[makeQuery(id+"F0.imprint","IMPRINT",EDGE,{"disambiguationData":[TD([[subQ2,-1.0]])],"derivedFrom":subQ1}),-1.0]])]});}
            var Q241;
            {var subQ0=sQuery(id+"F0.wireOp",EDGE,"E19");var subQ1=sQuery(id+"F0.wireOp",EDGE,"E1");var subQ2=makeQuery(id+"F0.imprint","INTERSECT",VERTEX,{"derivedFrom":[subQ1,subQ0]});Q241=makeQuery(id+"F0.imprint","IMPRINT",FACE,{"disambiguationData":[TD([[makeQuery(id+"F0.imprint","IMPRINT",EDGE,{"disambiguationData":[TD([[subQ2,-1.0]])],"derivedFrom":subQ1}),1.0]])]});}
            var Q242;
            {var subQ0=sQuery(id+"F0.wireOp",EDGE,"E64");var subQ1=sQuery(id+"F0.wireOp",EDGE,"E1");var subQ2=makeQuery(id+"F0.imprint","INTERSECT",VERTEX,{"derivedFrom":[subQ1,subQ0]});Q242=makeQuery(id+"F0.imprint","IMPRINT",FACE,{"disambiguationData":[TD([[makeQuery(id+"F0.imprint","IMPRINT",EDGE,{"disambiguationData":[TD([[subQ2,-1.0]])],"derivedFrom":subQ1}),-1.0]])]});}
            var Q243;
            {var subQ1=sQuery(id+"F0.wireOp",EDGE,"E1");var subQ9=sQuery(id+"F0.wireOp",EDGE,"E54");var subQ11=makeQuery(id+"F0.imprint","INTERSECT",VERTEX,{"derivedFrom":[subQ1,subQ9]});Q243=makeQuery(id+"F0.imprint","IMPRINT",FACE,{"disambiguationData":[TD([[makeQuery(id+"F0.imprint","IMPRINT",EDGE,{"disambiguationData":[TD([[subQ11,-1.0]])],"derivedFrom":subQ1}),1.0]])]});}
            var Q244;
            {var subQ5=sQuery(id+"F0.wireOp",EDGE,"E11");var subQ6=sQuery(id+"F0.wireOp",EDGE,"E1");var subQ7=makeQuery(id+"F0.imprint","INTERSECT",VERTEX,{"derivedFrom":[subQ6,subQ5]});Q244=makeQuery(id+"F0.imprint","IMPRINT",FACE,{"disambiguationData":[TD([[makeQuery(id+"F0.imprint","IMPRINT",EDGE,{"disambiguationData":[TD([[subQ7,-1.0]])],"derivedFrom":subQ6}),-1.0]])]});}
            var Q245;
            {var subQ0=sQuery(id+"F0.wireOp",EDGE,"E63");var subQ1=sQuery(id+"F0.wireOp",EDGE,"E2");var subQ2=makeQuery(id+"F0.imprint","INTERSECT",VERTEX,{"derivedFrom":[subQ1,subQ0]});Q245=makeQuery(id+"F0.imprint","IMPRINT",FACE,{"disambiguationData":[TD([[makeQuery(id+"F0.imprint","IMPRINT",EDGE,{"disambiguationData":[TD([[subQ2,-1.0]])],"derivedFrom":subQ1}),1.0]])]});}
            var Q246;
            {var subQ0=sQuery(id+"F0.wireOp",EDGE,"E53");var subQ1=sQuery(id+"F0.wireOp",EDGE,"E1");var subQ2=makeQuery(id+"F0.imprint","INTERSECT",VERTEX,{"derivedFrom":[subQ1,subQ0]});Q246=makeQuery(id+"F0.imprint","IMPRINT",FACE,{"disambiguationData":[TD([[makeQuery(id+"F0.imprint","IMPRINT",EDGE,{"disambiguationData":[TD([[subQ2,-1.0]])],"derivedFrom":subQ1}),-1.0]])]});}
            var Q247;
            {var subQ1=sQuery(id+"F0.wireOp",EDGE,"E2");var subQ5=sQuery(id+"F0.wireOp",EDGE,"E11");var subQ6=makeQuery(id+"F0.imprint","INTERSECT",VERTEX,{"derivedFrom":[subQ1,subQ5]});Q247=makeQuery(id+"F0.imprint","IMPRINT",FACE,{"disambiguationData":[TD([[makeQuery(id+"F0.imprint","IMPRINT",EDGE,{"disambiguationData":[TD([[subQ6,-1.0]])],"derivedFrom":subQ1}),1.0]])]});}
            var Q248;
            {var subQ0=sQuery(id+"F0.wireOp",EDGE,"E55");var subQ1=sQuery(id+"F0.wireOp",EDGE,"E2");var subQ2=makeQuery(id+"F0.imprint","INTERSECT",VERTEX,{"derivedFrom":[subQ1,subQ0]});Q248=makeQuery(id+"F0.imprint","IMPRINT",FACE,{"disambiguationData":[TD([[makeQuery(id+"F0.imprint","IMPRINT",EDGE,{"disambiguationData":[TD([[subQ2,-1.0]])],"derivedFrom":subQ1}),1.0]])]});}
            var Q249;
            {var subQ0=sQuery(id+"F0.wireOp",EDGE,"E60");var subQ1=sQuery(id+"F0.wireOp",EDGE,"E1");var subQ2=makeQuery(id+"F0.imprint","INTERSECT",VERTEX,{"derivedFrom":[subQ1,subQ0]});Q249=makeQuery(id+"F0.imprint","IMPRINT",FACE,{"disambiguationData":[TD([[makeQuery(id+"F0.imprint","IMPRINT",EDGE,{"disambiguationData":[TD([[subQ2,-1.0]])],"derivedFrom":subQ1}),-1.0]])]});}
            var Q250;
            {var subQ0=sQuery(id+"F0.wireOp",EDGE,"E50");var subQ1=sQuery(id+"F0.wireOp",EDGE,"E2");var subQ2=makeQuery(id+"F0.imprint","INTERSECT",VERTEX,{"derivedFrom":[subQ1,subQ0]});Q250=makeQuery(id+"F0.imprint","IMPRINT",FACE,{"disambiguationData":[TD([[makeQuery(id+"F0.imprint","IMPRINT",EDGE,{"disambiguationData":[TD([[subQ2,-1.0]])],"derivedFrom":subQ1}),1.0]])]});}
            var Q251;
            {var subQ0=sQuery(id+"F0.wireOp",EDGE,"E6");var subQ1=sQuery(id+"F0.wireOp",EDGE,"E1");var subQ2=makeQuery(id+"F0.imprint","INTERSECT",VERTEX,{"derivedFrom":[subQ1,subQ0]});Q251=makeQuery(id+"F0.imprint","IMPRINT",FACE,{"disambiguationData":[TD([[makeQuery(id+"F0.imprint","IMPRINT",EDGE,{"disambiguationData":[TD([[subQ2,-1.0]])],"derivedFrom":subQ1}),1.0]])]});}
            var Q252;
            {var subQ0=sQuery(id+"F0.wireOp",EDGE,"E51");var subQ1=sQuery(id+"F0.wireOp",EDGE,"E1");var subQ2=makeQuery(id+"F0.imprint","INTERSECT",VERTEX,{"derivedFrom":[subQ1,subQ0]});Q252=makeQuery(id+"F0.imprint","IMPRINT",FACE,{"disambiguationData":[TD([[makeQuery(id+"F0.imprint","IMPRINT",EDGE,{"disambiguationData":[TD([[subQ2,-1.0]])],"derivedFrom":subQ1}),-1.0]])]});}
            var Q253;
            {var subQ0=sQuery(id+"F0.wireOp",EDGE,"E64");var subQ1=sQuery(id+"F0.wireOp",EDGE,"E2");var subQ2=makeQuery(id+"F0.imprint","INTERSECT",VERTEX,{"derivedFrom":[subQ1,subQ0]});Q253=makeQuery(id+"F0.imprint","IMPRINT",FACE,{"disambiguationData":[TD([[makeQuery(id+"F0.imprint","IMPRINT",EDGE,{"disambiguationData":[TD([[subQ2,-1.0]])],"derivedFrom":subQ1}),1.0]])]});}
            var Q254;
            {var subQ0=sQuery(id+"F0.wireOp",EDGE,"E62");var subQ1=sQuery(id+"F0.wireOp",EDGE,"E1");var subQ2=makeQuery(id+"F0.imprint","INTERSECT",VERTEX,{"derivedFrom":[subQ1,subQ0]});Q254=makeQuery(id+"F0.imprint","IMPRINT",FACE,{"disambiguationData":[TD([[makeQuery(id+"F0.imprint","IMPRINT",EDGE,{"disambiguationData":[TD([[subQ2,-1.0]])],"derivedFrom":subQ1}),-1.0]])]});}
            var Q255;
            {var subQ0=sQuery(id+"F0.wireOp",EDGE,"E52");var subQ1=sQuery(id+"F0.wireOp",EDGE,"E2");var subQ2=makeQuery(id+"F0.imprint","INTERSECT",VERTEX,{"derivedFrom":[subQ1,subQ0]});Q255=makeQuery(id+"F0.imprint","IMPRINT",FACE,{"disambiguationData":[TD([[makeQuery(id+"F0.imprint","IMPRINT",EDGE,{"disambiguationData":[TD([[subQ2,-1.0]])],"derivedFrom":subQ1}),1.0]])]});}
            var Q256;
            {var subQ0=sQuery(id+"F0.wireOp",EDGE,"E54");var subQ1=sQuery(id+"F0.wireOp",EDGE,"E2");var subQ2=makeQuery(id+"F0.imprint","INTERSECT",VERTEX,{"derivedFrom":[subQ1,subQ0]});Q256=makeQuery(id+"F0.imprint","IMPRINT",FACE,{"disambiguationData":[TD([[makeQuery(id+"F0.imprint","IMPRINT",EDGE,{"disambiguationData":[TD([[subQ2,-1.0]])],"derivedFrom":subQ1}),1.0]])]});}
            var Q257;
            {var subQ0=sQuery(id+"F0.wireOp",EDGE,"E51");var subQ1=sQuery(id+"F0.wireOp",EDGE,"E2");var subQ2=makeQuery(id+"F0.imprint","INTERSECT",VERTEX,{"derivedFrom":[subQ1,subQ0]});Q257=makeQuery(id+"F0.imprint","IMPRINT",FACE,{"disambiguationData":[TD([[makeQuery(id+"F0.imprint","IMPRINT",EDGE,{"disambiguationData":[TD([[subQ2,-1.0]])],"derivedFrom":subQ1}),1.0]])]});}
            var Q258;
            {var subQ0=sQuery(id+"F0.wireOp",EDGE,"E17");var subQ1=sQuery(id+"F0.wireOp",EDGE,"E1");var subQ2=makeQuery(id+"F0.imprint","INTERSECT",VERTEX,{"derivedFrom":[subQ1,subQ0]});Q258=makeQuery(id+"F0.imprint","IMPRINT",FACE,{"disambiguationData":[TD([[makeQuery(id+"F0.imprint","IMPRINT",EDGE,{"disambiguationData":[TD([[subQ2,-1.0]])],"derivedFrom":subQ1}),1.0]])]});}
            var Q259;
            {var subQ0=sQuery(id+"F0.wireOp",EDGE,"E7");var subQ1=sQuery(id+"F0.wireOp",EDGE,"E1");var subQ2=makeQuery(id+"F0.imprint","INTERSECT",VERTEX,{"derivedFrom":[subQ1,subQ0]});Q259=makeQuery(id+"F0.imprint","IMPRINT",FACE,{"disambiguationData":[TD([[makeQuery(id+"F0.imprint","IMPRINT",EDGE,{"disambiguationData":[TD([[subQ2,-1.0]])],"derivedFrom":subQ1}),1.0]])]});}
            var Q260;
            {var subQ0=sQuery(id+"F0.wireOp",EDGE,"E9");var subQ1=sQuery(id+"F0.wireOp",EDGE,"E1");var subQ2=makeQuery(id+"F0.imprint","INTERSECT",VERTEX,{"derivedFrom":[subQ1,subQ0]});Q260=makeQuery(id+"F0.imprint","IMPRINT",FACE,{"disambiguationData":[TD([[makeQuery(id+"F0.imprint","IMPRINT",EDGE,{"disambiguationData":[TD([[subQ2,-1.0]])],"derivedFrom":subQ1}),1.0]])]});}
            var Q261;
            {var subQ0=sQuery(id+"F0.wireOp",EDGE,"E60");var subQ1=sQuery(id+"F0.wireOp",EDGE,"E2");var subQ2=makeQuery(id+"F0.imprint","INTERSECT",VERTEX,{"derivedFrom":[subQ1,subQ0]});Q261=makeQuery(id+"F0.imprint","IMPRINT",FACE,{"disambiguationData":[TD([[makeQuery(id+"F0.imprint","IMPRINT",EDGE,{"disambiguationData":[TD([[subQ2,-1.0]])],"derivedFrom":subQ1}),1.0]])]});}
            var Q262;
            {var subQ0=sQuery(id+"F0.wireOp",EDGE,"E3");var subQ1=sQuery(id+"F0.wireOp",EDGE,"E2");var subQ2=makeQuery(id+"F0.imprint","INTERSECT",VERTEX,{"derivedFrom":[subQ1,subQ0]});Q262=makeQuery(id+"F0.imprint","IMPRINT",FACE,{"disambiguationData":[TD([[makeQuery(id+"F0.imprint","IMPRINT",EDGE,{"disambiguationData":[TD([[subQ2,-1.0]])],"derivedFrom":subQ1}),-1.0]])]});}
            var Q263;
            {var subQ0=sQuery(id+"F0.wireOp",EDGE,"E13");var subQ1=sQuery(id+"F0.wireOp",EDGE,"E1");var subQ2=makeQuery(id+"F0.imprint","INTERSECT",VERTEX,{"derivedFrom":[subQ1,subQ0]});Q263=makeQuery(id+"F0.imprint","IMPRINT",FACE,{"disambiguationData":[TD([[makeQuery(id+"F0.imprint","IMPRINT",EDGE,{"disambiguationData":[TD([[subQ2,-1.0]])],"derivedFrom":subQ1}),1.0]])]});}
            var Q264;
            {var subQ0=sQuery(id+"F0.wireOp",EDGE,"E2");var subQ1=sQuery(id+"F0.wireOp",EDGE,"E1");var subQ2=makeQuery(id+"F0.imprint","INTERSECT",VERTEX,{"derivedFrom":[subQ1,subQ0]});Q264=makeQuery(id+"F0.imprint","IMPRINT",FACE,{"disambiguationData":[TD([[makeQuery(id+"F0.imprint","IMPRINT",EDGE,{"disambiguationData":[TD([[subQ2,-1.0]])],"derivedFrom":subQ1}),-1.0]])]});}
            var Q265;
            {var subQ0=sQuery(id+"F0.wireOp",EDGE,"E53");var subQ1=sQuery(id+"F0.wireOp",EDGE,"E2");var subQ2=makeQuery(id+"F0.imprint","INTERSECT",VERTEX,{"derivedFrom":[subQ1,subQ0]});Q265=makeQuery(id+"F0.imprint","IMPRINT",FACE,{"disambiguationData":[TD([[makeQuery(id+"F0.imprint","IMPRINT",EDGE,{"disambiguationData":[TD([[subQ2,-1.0]])],"derivedFrom":subQ1}),1.0]])]});}
            var Q266;
            {var subQ0=sQuery(id+"F0.wireOp",EDGE,"E52");var subQ1=sQuery(id+"F0.wireOp",EDGE,"E1");var subQ2=makeQuery(id+"F0.imprint","INTERSECT",VERTEX,{"derivedFrom":[subQ1,subQ0]});Q266=makeQuery(id+"F0.imprint","IMPRINT",FACE,{"disambiguationData":[TD([[makeQuery(id+"F0.imprint","IMPRINT",EDGE,{"disambiguationData":[TD([[subQ2,-1.0]])],"derivedFrom":subQ1}),-1.0]])]});}
            var Q267;
            {var subQ0=sQuery(id+"F0.wireOp",EDGE,"E55");var subQ1=sQuery(id+"F0.wireOp",EDGE,"E1");var subQ2=makeQuery(id+"F0.imprint","INTERSECT",VERTEX,{"derivedFrom":[subQ1,subQ0]});Q267=makeQuery(id+"F0.imprint","IMPRINT",FACE,{"disambiguationData":[TD([[makeQuery(id+"F0.imprint","IMPRINT",EDGE,{"disambiguationData":[TD([[subQ2,-1.0]])],"derivedFrom":subQ1}),-1.0]])]});}
            var Q268;
            {var subQ0=sQuery(id+"F0.wireOp",EDGE,"E5");var subQ1=sQuery(id+"F0.wireOp",EDGE,"E2");var subQ2=makeQuery(id+"F0.imprint","INTERSECT",VERTEX,{"derivedFrom":[subQ1,subQ0]});Q268=makeQuery(id+"F0.imprint","IMPRINT",FACE,{"disambiguationData":[TD([[makeQuery(id+"F0.imprint","IMPRINT",EDGE,{"disambiguationData":[TD([[subQ2,-1.0]])],"derivedFrom":subQ1}),-1.0]])]});}
            var Q269;
            {var subQ0=sQuery(id+"F0.wireOp",EDGE,"E24");var subQ1=sQuery(id+"F0.wireOp",EDGE,"E1");var subQ2=makeQuery(id+"F0.imprint","INTERSECT",VERTEX,{"derivedFrom":[subQ1,subQ0]});Q269=makeQuery(id+"F0.imprint","IMPRINT",FACE,{"disambiguationData":[TD([[makeQuery(id+"F0.imprint","IMPRINT",EDGE,{"disambiguationData":[TD([[subQ2,-1.0]])],"derivedFrom":subQ1}),1.0]])]});}
            var Q270;
            {var subQ0=sQuery(id+"F0.wireOp",EDGE,"E19");var subQ1=sQuery(id+"F0.wireOp",EDGE,"E2");var subQ2=makeQuery(id+"F0.imprint","INTERSECT",VERTEX,{"derivedFrom":[subQ1,subQ0]});Q270=makeQuery(id+"F0.imprint","IMPRINT",FACE,{"disambiguationData":[TD([[makeQuery(id+"F0.imprint","IMPRINT",EDGE,{"disambiguationData":[TD([[subQ2,-1.0]])],"derivedFrom":subQ1}),-1.0]])]});}
            var Q271;
            {var subQ0=sQuery(id+"F0.wireOp",EDGE,"E50");var subQ1=sQuery(id+"F0.wireOp",EDGE,"E1");var subQ2=makeQuery(id+"F0.imprint","INTERSECT",VERTEX,{"derivedFrom":[subQ1,subQ0]});Q271=makeQuery(id+"F0.imprint","IMPRINT",FACE,{"disambiguationData":[TD([[makeQuery(id+"F0.imprint","IMPRINT",EDGE,{"disambiguationData":[TD([[subQ2,-1.0]])],"derivedFrom":subQ1}),-1.0]])]});}
            var Q272;
            {var subQ0=sQuery(id+"F0.wireOp",EDGE,"E11");var subQ1=sQuery(id+"F0.wireOp",EDGE,"E2");var subQ2=makeQuery(id+"F0.imprint","INTERSECT",VERTEX,{"derivedFrom":[subQ1,subQ0]});Q272=makeQuery(id+"F0.imprint","IMPRINT",FACE,{"disambiguationData":[TD([[makeQuery(id+"F0.imprint","IMPRINT",EDGE,{"disambiguationData":[TD([[subQ2,-1.0]])],"derivedFrom":subQ1}),-1.0]])]});}
            var Q273;
            {var subQ0=sQuery(id+"F0.wireOp",EDGE,"E49");var subQ1=sQuery(id+"F0.wireOp",EDGE,"E1");var subQ2=makeQuery(id+"F0.imprint","INTERSECT",VERTEX,{"derivedFrom":[subQ1,subQ0]});Q273=makeQuery(id+"F0.imprint","IMPRINT",FACE,{"disambiguationData":[TD([[makeQuery(id+"F0.imprint","IMPRINT",EDGE,{"disambiguationData":[TD([[subQ2,-1.0]])],"derivedFrom":subQ1}),-1.0]])]});}
            var Q274;
            {var subQ0=sQuery(id+"F0.wireOp",EDGE,"E61");var subQ1=sQuery(id+"F0.wireOp",EDGE,"E1");var subQ2=makeQuery(id+"F0.imprint","INTERSECT",VERTEX,{"derivedFrom":[subQ1,subQ0]});Q274=makeQuery(id+"F0.imprint","IMPRINT",FACE,{"disambiguationData":[TD([[makeQuery(id+"F0.imprint","IMPRINT",EDGE,{"disambiguationData":[TD([[subQ2,-1.0]])],"derivedFrom":subQ1}),-1.0]])]});}
            var Q275;
            {var subQ0=sQuery(id+"F0.wireOp",EDGE,"E49");var subQ1=sQuery(id+"F0.wireOp",EDGE,"E2");var subQ2=makeQuery(id+"F0.imprint","INTERSECT",VERTEX,{"derivedFrom":[subQ1,subQ0]});Q275=makeQuery(id+"F0.imprint","IMPRINT",FACE,{"disambiguationData":[TD([[makeQuery(id+"F0.imprint","IMPRINT",EDGE,{"disambiguationData":[TD([[subQ2,-1.0]])],"derivedFrom":subQ1}),1.0]])]});}
            var Q276;
            {var subQ5=sQuery(id+"F0.wireOp",EDGE,"E1");var subQ7=sQuery(id+"F0.wireOp",EDGE,"E55");var subQ9=makeQuery(id+"F0.imprint","INTERSECT",VERTEX,{"derivedFrom":[subQ5,subQ7]});Q276=makeQuery(id+"F0.imprint","IMPRINT",FACE,{"disambiguationData":[TD([[makeQuery(id+"F0.imprint","IMPRINT",EDGE,{"disambiguationData":[TD([[subQ9,-1.0]])],"derivedFrom":subQ5}),1.0]])]});}
            var Q277;
            {var subQ0=sQuery(id+"F0.wireOp",EDGE,"E54");var subQ1=sQuery(id+"F0.wireOp",EDGE,"E1");var subQ2=makeQuery(id+"F0.imprint","INTERSECT",VERTEX,{"derivedFrom":[subQ1,subQ0]});Q277=makeQuery(id+"F0.imprint","IMPRINT",FACE,{"disambiguationData":[TD([[makeQuery(id+"F0.imprint","IMPRINT",EDGE,{"disambiguationData":[TD([[subQ2,-1.0]])],"derivedFrom":subQ1}),-1.0]])]});}
            var Q278;
            {var subQ0=sQuery(id+"F0.wireOp",EDGE,"E11");var subQ1=sQuery(id+"F0.wireOp",EDGE,"E1");var subQ2=makeQuery(id+"F0.imprint","INTERSECT",VERTEX,{"derivedFrom":[subQ1,subQ0]});Q278=makeQuery(id+"F0.imprint","IMPRINT",FACE,{"disambiguationData":[TD([[makeQuery(id+"F0.imprint","IMPRINT",EDGE,{"disambiguationData":[TD([[subQ2,-1.0]])],"derivedFrom":subQ1}),1.0]])]});}
            var Q279;
            {var subQ0=sQuery(id+"F0.wireOp",EDGE,"E61");var subQ1=sQuery(id+"F0.wireOp",EDGE,"E2");var subQ2=makeQuery(id+"F0.imprint","INTERSECT",VERTEX,{"derivedFrom":[subQ1,subQ0]});Q279=makeQuery(id+"F0.imprint","IMPRINT",FACE,{"disambiguationData":[TD([[makeQuery(id+"F0.imprint","IMPRINT",EDGE,{"disambiguationData":[TD([[subQ2,-1.0]])],"derivedFrom":subQ1}),1.0]])]});}
            var Q280;
            {var subQ0=sQuery(id+"F0.wireOp",EDGE,"E48");var subQ1=sQuery(id+"F0.wireOp",EDGE,"E1");var subQ2=makeQuery(id+"F0.imprint","INTERSECT",VERTEX,{"derivedFrom":[subQ1,subQ0]});Q280=makeQuery(id+"F0.imprint","IMPRINT",FACE,{"disambiguationData":[TD([[makeQuery(id+"F0.imprint","IMPRINT",EDGE,{"disambiguationData":[TD([[subQ2,-1.0]])],"derivedFrom":subQ1}),-1.0]])]});}
            var Q281;
            {var subQ0=sQuery(id+"F0.wireOp",EDGE,"E4");var subQ1=sQuery(id+"F0.wireOp",EDGE,"E2");var subQ2=makeQuery(id+"F0.imprint","INTERSECT",VERTEX,{"derivedFrom":[subQ1,subQ0]});Q281=makeQuery(id+"F0.imprint","IMPRINT",FACE,{"disambiguationData":[TD([[makeQuery(id+"F0.imprint","IMPRINT",EDGE,{"disambiguationData":[TD([[subQ2,-1.0]])],"derivedFrom":subQ1}),-1.0]])]});}
            var Q282;
            {var subQ0=sQuery(id+"F0.wireOp",EDGE,"E1");var subQ3=sQuery(id+"F0.wireOp",EDGE,"E47");var subQ5=makeQuery(id+"F0.imprint","INTERSECT",VERTEX,{"derivedFrom":[subQ0,subQ3]});Q282=makeQuery(id+"F0.imprint","IMPRINT",FACE,{"disambiguationData":[TD([[makeQuery(id+"F0.imprint","IMPRINT",EDGE,{"disambiguationData":[TD([[subQ5,-1.0]])],"derivedFrom":subQ0}),-1.0]])]});}
            var Q283;
            {var subQ0=sQuery(id+"F0.wireOp",EDGE,"E63");var subQ1=sQuery(id+"F0.wireOp",EDGE,"E1");var subQ2=makeQuery(id+"F0.imprint","INTERSECT",VERTEX,{"derivedFrom":[subQ1,subQ0]});Q283=makeQuery(id+"F0.imprint","IMPRINT",FACE,{"disambiguationData":[TD([[makeQuery(id+"F0.imprint","IMPRINT",EDGE,{"disambiguationData":[TD([[subQ2,-1.0]])],"derivedFrom":subQ1}),-1.0]])]});}
            extrude(context, id + "F1", {"entities" : qUnion([Q0, Q1, Q2, Q3, Q4, Q5, Q6, Q7, Q8, Q9, Q10, Q11, Q12, Q13, Q14, Q15, Q16, Q17, Q18, Q19, Q20, Q21, Q22, Q23, Q24, Q25, Q26, Q27, Q28, Q29, Q30, Q31, Q32, Q33, Q34, Q35, Q36, Q37, Q38, Q39, Q40, Q41, Q42, Q43, Q44, Q45, Q46, Q47, Q48, Q49, Q50, Q51, Q52, Q53, Q54, Q55, Q56, Q57, Q58, Q59, Q60, Q61, Q62, Q63, Q64, Q65, Q66, Q67, Q68, Q69, Q70, Q71, Q72, Q73, Q74, Q75, Q76, Q77, Q78, Q79, Q80, Q81, Q82, Q83, Q84, Q85, Q86, Q87, Q88, Q89, Q90, Q91, Q92, Q93, Q94, Q95, Q96, Q97, Q98, Q99, Q100, Q101, Q102, Q103, Q104, Q105, Q106, Q107, Q108, Q109, Q110, Q111, Q112, Q113, Q114, Q115, Q116, Q117, Q118, Q119, Q120, Q121, Q122, Q123, Q124, Q125, Q126, Q127, Q128, Q129, Q130, Q131, Q132, Q133, Q134, Q135, Q136, Q137, Q138, Q139, Q140, Q141, Q142, Q143, Q144, Q145, Q146, Q147, Q148, Q149, Q150, Q151, Q152, Q153, Q154, Q155, Q156, Q157, Q158, Q159, Q160, Q161, Q162, Q163, Q164, Q165, Q166, Q167, Q168, Q169, Q170, Q171, Q172, Q173, Q174, Q175, Q176, Q177, Q178, Q179, Q180, Q181, Q182, Q183, Q184, Q185, Q186, Q187, Q188, Q189, Q190, Q191, Q192, Q193, Q194, Q195, Q196, Q197, Q198, Q199, Q200, Q201, Q202, Q203, Q204, Q205, Q206, Q207, Q208, Q209, Q210, Q211, Q212, Q213, Q214, Q215, Q216, Q217, Q218, Q219, Q220, Q221, Q222, Q223, Q224, Q225, Q226, Q227, Q228, Q229, Q230, Q231, Q232, Q233, Q234, Q235, Q236, Q237, Q238, Q239, Q240, Q241, Q242, Q243, Q244, Q245, Q246, Q247, Q248, Q249, Q250, Q251, Q252, Q253, Q254, Q255, Q256, Q257, Q258, Q259, Q260, Q261, Q262, Q263, Q264, Q265, Q266, Q267, Q268, Q269, Q270, Q271, Q272, Q273, Q274, Q275, Q276, Q277, Q278, Q279, Q280, Q281, Q282, Q283]), "depth" : 3.3 * mm, "offsetDistance" : 25.4 * mm});
        }
    });
